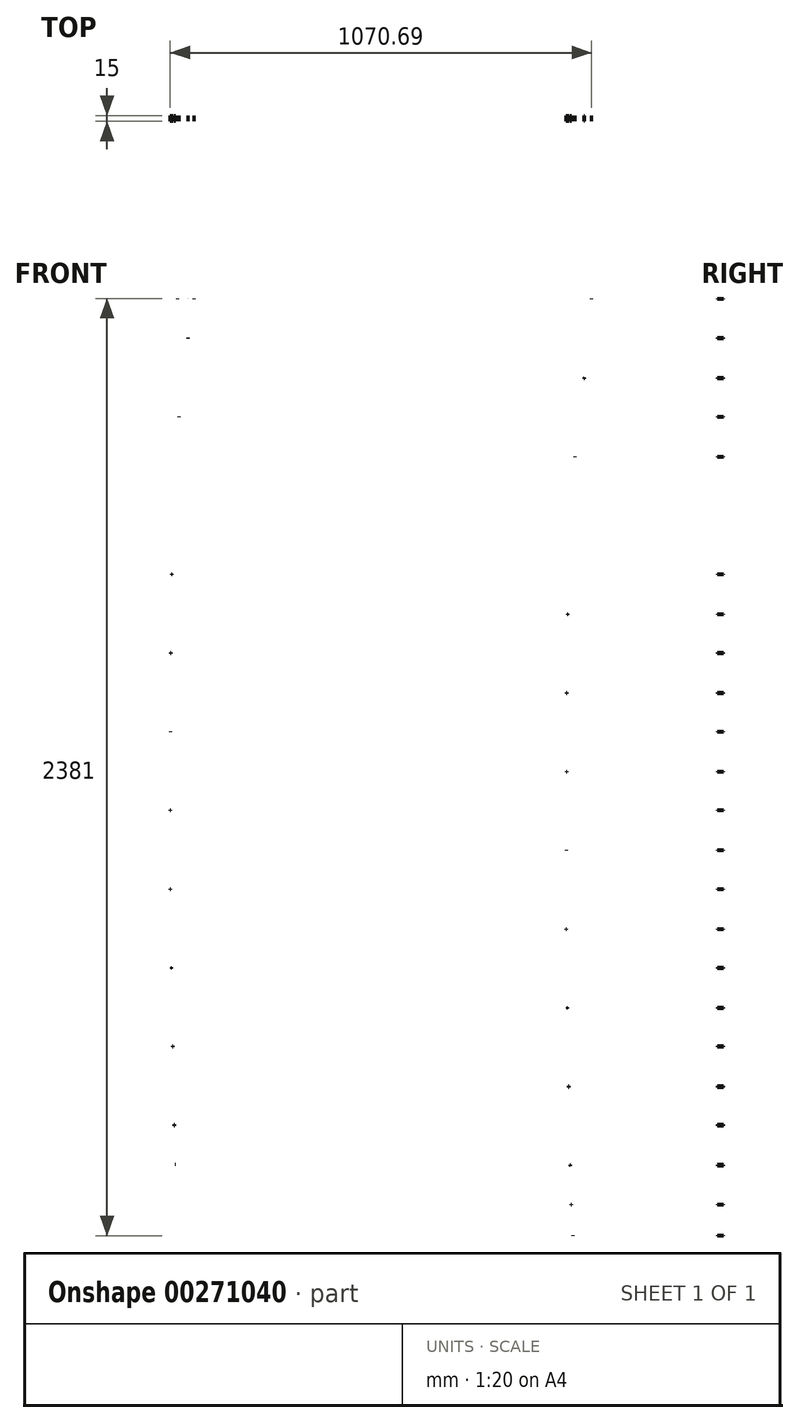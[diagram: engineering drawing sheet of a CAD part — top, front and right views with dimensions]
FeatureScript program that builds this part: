
annotation { "Feature Type Name" : "Feature", "Feature Type Description" : "" }
export const myFeature = defineFeature(function(context is Context, id is Id, definition is map)
    precondition{}
    {
        {
            var Q0;
            Q0=qCreatedBy(makeId("Front.planeOp"),FACE);
            var sketch = newSketch(context, id + "F0", { "sketchPlane" : qUnion([Q0])});
            skPoint(sketch, "E0", {"position": v(2171.02, -1257.1) * mm});
            skPoint(sketch, "E1", {"position": v(2158.22, -1157.1) * mm});
            skPoint(sketch, "E2", {"position": v(2144, -957.1) * mm});
            skPoint(sketch, "E3", {"position": v(2135.3, -757.1) * mm});
            skPoint(sketch, "E4", {"position": v(2123.54, -557.1) * mm});
            skPoint(sketch, "E5", {"position": v(2120.16, -357.1) * mm});
            skPoint(sketch, "E6", {"position": v(2123.04, -157.1) * mm});
            skPoint(sketch, "E7", {"position": v(2124, 42.9) * mm});
            skPoint(sketch, "E8", {"position": v(2129.38, 242.9) * mm});
            skPoint(sketch, "E9", {"position": v(2143.08, 442.9) * mm});
            skPoint(sketch, "E10", {"position": v(2163.32, 642.9) * mm});
            skPoint(sketch, "E11", {"position": v(2247.52, 842.9) * mm});
            skPoint(sketch, "E12", {"position": v(2193.17, 842.9) * mm});
            skPoint(sketch, "E13", {"position": v(2259.83, 942.9) * mm});
            skPoint(sketch, "E14", {"position": v(2213.09, 942.9) * mm});
            skPoint(sketch, "E15", {"position": v(2213.13, 942.9) * mm});
            skLineSegment(sketch, "E16", {"start": v(2259.83, 942.9) * mm, "end": v(2213.09, 942.9) * mm});
            skLineSegment(sketch, "E17", {"start": v(2247.52, 842.9) * mm, "end": v(2193.17, 842.9) * mm});
            skLineSegment(sketch, "E18", {"start": v(2220.35, 842.9) * mm, "end": v(2247.52, 842.9) * mm});
            skLineSegment(sketch, "E19", {"start": v(2226.63, 642.9) * mm, "end": v(2163.32, 642.9) * mm});
            skLineSegment(sketch, "E20", {"start": v(2216.48, 442.9) * mm, "end": v(2143.08, 442.9) * mm});
            skLineSegment(sketch, "E21", {"start": v(2209.4, 242.9) * mm, "end": v(2129.38, 242.9) * mm});
            skLineSegment(sketch, "E22", {"start": v(2206.83, 42.9) * mm, "end": v(2124, 42.9) * mm});
            skLineSegment(sketch, "E23", {"start": v(2206.87, -157.1) * mm, "end": v(2123.04, -157.1) * mm});
            skLineSegment(sketch, "E24", {"start": v(2206.44, -357.1) * mm, "end": v(2120.16, -357.1) * mm});
            skLineSegment(sketch, "E25", {"start": v(2205.72, -557.1) * mm, "end": v(2123.54, -557.1) * mm});
            skLineSegment(sketch, "E26", {"start": v(2208.01, -757.1) * mm, "end": v(2135.3, -757.1) * mm});
            skLineSegment(sketch, "E27", {"start": v(2210.87, -957.1) * mm, "end": v(2144, -957.1) * mm});
            skLineSegment(sketch, "E28", {"start": v(2213.68, -1157.1) * mm, "end": v(2158.22, -1157.1) * mm});
            skLineSegment(sketch, "E29", {"start": v(2214.8, -1257.1) * mm, "end": v(2171.02, -1257.1) * mm});
            skLineSegment(sketch, "E30", {"start": v(2213.09, 942.9) * mm, "end": v(2217.48, 942.9) * mm});
            skLineSegment(sketch, "E31", {"start": v(2217.48, 942.9) * mm, "end": v(2258.48, 942.9) * mm});
            skLineSegment(sketch, "E32", {"start": v(2258.48, 942.9) * mm, "end": v(2259.83, 942.9) * mm});
            skLineSegment(sketch, "E33", {"start": v(2259.75, 1046.85) * mm, "end": v(2259.75, 1077.73) * mm});
            skLineSegment(sketch, "E34", {"start": v(2273.7, 1034.65) * mm, "end": v(2273.7, 1081.36) * mm});
            skFitSpline(sketch, "E35", {"points": [v(2258.48, 942.9) * mm, v(2266.12, 990.74) * mm, v(2269.2, 1016.45) * mm, v(2266.37, 1037.52) * mm, v(2259.75, 1046.85) * mm, v(2248.64, 1041.9) * mm, v(2241.7, 1029.55) * mm, v(2229.88, 994.85) * mm, v(2217.48, 942.9) * mm], "startDerivative": vector(69.99, 299.65) * mm, "endDerivative": vector(-63.8, -297.22) * mm});
            skLineSegment(sketch, "E36", {"start": v(2193.17, 842.9) * mm, "end": v(2198.84, 842.9) * mm});
            skLineSegment(sketch, "E37", {"start": v(2198.84, 842.9) * mm, "end": v(2243.84, 842.9) * mm});
            skLineSegment(sketch, "E38", {"start": v(2243.84, 842.9) * mm, "end": v(2247.52, 842.9) * mm});
            skLineSegment(sketch, "E39", {"start": v(2226.63, 642.9) * mm, "end": v(2220.48, 642.9) * mm});
            skLineSegment(sketch, "E40", {"start": v(2220.48, 642.9) * mm, "end": v(2169.47, 642.9) * mm});
            skLineSegment(sketch, "E41", {"start": v(2169.47, 642.9) * mm, "end": v(2163.32, 642.9) * mm});
            skLineSegment(sketch, "E42", {"start": v(2209.28, 442.9) * mm, "end": v(2150.28, 442.9) * mm});
            skLineSegment(sketch, "E43", {"start": v(2150.28, 442.9) * mm, "end": v(2143.08, 442.9) * mm});
            skLineSegment(sketch, "E44", {"start": v(2201.9, 242.9) * mm, "end": v(2136.88, 242.9) * mm});
            skLineSegment(sketch, "E45", {"start": v(2136.88, 242.9) * mm, "end": v(2129.38, 242.9) * mm});
            skLineSegment(sketch, "E46", {"start": v(2199.43, 42.9) * mm, "end": v(2131.4, 42.9) * mm});
            skLineSegment(sketch, "E47", {"start": v(2131.4, 42.9) * mm, "end": v(2124, 42.9) * mm});
            skLineSegment(sketch, "E48", {"start": v(2199.16, -157.1) * mm, "end": v(2130.75, -157.1) * mm});
            skLineSegment(sketch, "E49", {"start": v(2130.75, -157.1) * mm, "end": v(2123.04, -157.1) * mm});
            skLineSegment(sketch, "E50", {"start": v(2198.3, -357.1) * mm, "end": v(2128.3, -357.1) * mm});
            skLineSegment(sketch, "E51", {"start": v(2128.3, -357.1) * mm, "end": v(2120.16, -357.1) * mm});
            skLineSegment(sketch, "E52", {"start": v(2198.13, -557.1) * mm, "end": v(2131.13, -557.1) * mm});
            skLineSegment(sketch, "E53", {"start": v(2131.13, -557.1) * mm, "end": v(2123.54, -557.1) * mm});
            skLineSegment(sketch, "E54", {"start": v(2201.35, -757.1) * mm, "end": v(2141.95, -757.1) * mm});
            skLineSegment(sketch, "E55", {"start": v(2141.95, -757.1) * mm, "end": v(2135.3, -757.1) * mm});
            skLineSegment(sketch, "E56", {"start": v(2204.43, -957.1) * mm, "end": v(2150.44, -957.1) * mm});
            skLineSegment(sketch, "E57", {"start": v(2150.44, -957.1) * mm, "end": v(2144, -957.1) * mm});
            skLineSegment(sketch, "E58", {"start": v(2208.34, -1157.1) * mm, "end": v(2163.56, -1157.1) * mm});
            skLineSegment(sketch, "E59", {"start": v(2163.56, -1157.1) * mm, "end": v(2158.22, -1157.1) * mm});
            skLineSegment(sketch, "E60", {"start": v(2210.71, -1257.1) * mm, "end": v(2175.1, -1257.1) * mm});
            skLineSegment(sketch, "E61", {"start": v(2175.1, -1257.1) * mm, "end": v(2171.02, -1257.1) * mm});
            skFitSpline(sketch, "E62", {"points": [v(2258.48, 942.9) * mm, v(2243.84, 842.9) * mm, v(2220.48, 642.9) * mm, v(2209.28, 442.9) * mm, v(2201.9, 242.9) * mm, v(2199.43, 42.9) * mm, v(2199.16, -157.1) * mm, v(2198.3, -357.1) * mm, v(2198.13, -557.1) * mm, v(2201.35, -757.1) * mm, v(2204.43, -957.1) * mm, v(2208.34, -1157.1) * mm, v(2210.71, -1257.1) * mm], "startDerivative": vector(-207.13, -1457.4) * mm, "endDerivative": vector(36.18, -1464.69) * mm});
            skFitSpline(sketch, "E63", {"points": [v(2210.71, -1257.1) * mm, v(2212.63, -1286.96) * mm, v(2214.74, -1318.98) * mm], "startDerivative": vector(3.84, -60.24) * mm, "endDerivative": vector(4.21, -63.47) * mm});
            skFitSpline(sketch, "E64", {"points": [v(2217.48, 942.9) * mm, v(2198.84, 842.9) * mm, v(2169.47, 642.9) * mm, v(2150.28, 442.9) * mm, v(2136.88, 242.9) * mm, v(2131.4, 42.9) * mm, v(2130.75, -157.1) * mm, v(2128.3, -357.1) * mm, v(2131.13, -557.1) * mm, v(2141.95, -757.1) * mm, v(2150.44, -957.1) * mm, v(2163.56, -1157.1) * mm, v(2175.1, -1257.1) * mm], "startDerivative": vector(-284.6, -1452.48) * mm, "endDerivative": vector(190.25, -1460.4) * mm});
            skFitSpline(sketch, "E65", {"points": [v(2175.1, -1257.1) * mm, v(2181.76, -1302.3) * mm, v(2183.86, -1323.32) * mm, v(2189.33, -1345.61) * mm, v(2194.8, -1356.55) * mm, v(2201.95, -1361.07) * mm, v(2209.1, -1357.4) * mm, v(2214.14, -1347.72) * mm, v(2215.4, -1335.52) * mm, v(2214.74, -1318.98) * mm], "startDerivative": vector(43.58, -267.95) * mm, "endDerivative": vector(-8.77, 152.7) * mm});
            skLineSegment(sketch, "E66", {"start": v(2258.48, 942.9) * mm, "end": v(2237.98, 942.9) * mm});
            skLineSegment(sketch, "E67", {"start": v(2131.4, 42.9) * mm, "end": v(2037.97, 42.9) * mm});
            skLineSegment(sketch, "E68", {"start": v(2037.97, 42.9) * mm, "end": v(2037.97, -1620.04) * mm});
            skLineSegment(sketch, "E69", {"start": v(2037.97, 42.9) * mm, "end": v(2037.97, 1196.3) * mm});
            skLineSegment(sketch, "E70", {"start": v(2217.48, 942.9) * mm, "end": v(2037.97, 942.9) * mm});
            skLineSegment(sketch, "E71", {"start": v(2198.84, 842.9) * mm, "end": v(2037.97, 842.9) * mm});
            skLineSegment(sketch, "E72", {"start": v(2169.47, 642.9) * mm, "end": v(2037.97, 642.9) * mm});
            skLineSegment(sketch, "E73", {"start": v(2150.28, 442.9) * mm, "end": v(2037.97, 442.9) * mm});
            skLineSegment(sketch, "E74", {"start": v(2136.88, 242.9) * mm, "end": v(2037.97, 242.9) * mm});
            skLineSegment(sketch, "E75", {"start": v(2130.75, -157.1) * mm, "end": v(2037.97, -157.1) * mm});
            skLineSegment(sketch, "E76", {"start": v(2128.3, -357.1) * mm, "end": v(2037.97, -357.1) * mm});
            skLineSegment(sketch, "E77", {"start": v(2131.13, -557.1) * mm, "end": v(2037.97, -557.1) * mm});
            skLineSegment(sketch, "E78", {"start": v(2141.95, -757.1) * mm, "end": v(2037.97, -757.1) * mm});
            skLineSegment(sketch, "E79", {"start": v(2150.44, -957.1) * mm, "end": v(2037.97, -957.1) * mm});
            skLineSegment(sketch, "E80", {"start": v(2163.56, -1157.1) * mm, "end": v(2037.97, -1157.1) * mm});
            skLineSegment(sketch, "E81", {"start": v(2175.1, -1257.1) * mm, "end": v(2037.97, -1257.1) * mm});
            skLineSegment(sketch, "E82", {"start": v(2201.95, -1361.07) * mm, "end": v(2037.97, -1361.07) * mm});
            skLineSegment(sketch, "E83", {"start": v(2037.97, -1257.1) * mm, "end": v(2037.97, -1282.1) * mm});
            skLineSegment(sketch, "E84", {"start": v(2037.97, -1282.1) * mm, "end": v(2037.97, -1311.07) * mm});
            skLineSegment(sketch, "E85", {"start": v(2037.97, -1311.07) * mm, "end": v(2037.97, -1336.07) * mm});
            skLineSegment(sketch, "E86", {"start": v(2037.97, -1336.07) * mm, "end": v(2037.97, -1361.07) * mm});
            skLineSegment(sketch, "E87", {"start": v(2037.97, -1336.07) * mm, "end": v(2186.54, -1336.07) * mm});
            skLineSegment(sketch, "E88", {"start": v(2215.4, -1335.52) * mm, "end": v(2186.54, -1336.07) * mm});
            skLineSegment(sketch, "E89", {"start": v(2259.75, 1046.85) * mm, "end": v(2247.06, 1046.85) * mm});
            skLineSegment(sketch, "E90", {"start": v(2037.97, 1046.85) * mm, "end": v(2037.97, 1021.87) * mm});
            skLineSegment(sketch, "E91", {"start": v(2037.97, 1021.87) * mm, "end": v(2238.81, 1021.87) * mm});
            skLineSegment(sketch, "E92", {"start": v(2128.3, -357.1) * mm, "end": v(2128.3, 1046.85) * mm});
            skLineSegment(sketch, "E93", {"start": v(2128.3, -357.1) * mm, "end": v(2128.3, -1361.07) * mm});
            skLineSegment(sketch, "E94", {"start": v(2128.3, -1361.07) * mm, "end": v(2128.3, 1046.85) * mm});
            skLineSegment(sketch, "E95", {"start": v(2258.48, 942.9) * mm, "end": v(2243.48, 942.9) * mm});
            skLineSegment(sketch, "E96", {"start": v(2243.84, 842.9) * mm, "end": v(2228.84, 842.9) * mm});
            skLineSegment(sketch, "E97", {"start": v(2220.48, 642.9) * mm, "end": v(2205.48, 642.9) * mm});
            skLineSegment(sketch, "E98", {"start": v(2209.28, 442.9) * mm, "end": v(2194.28, 442.9) * mm});
            skLineSegment(sketch, "E99", {"start": v(2201.9, 242.9) * mm, "end": v(2186.9, 242.9) * mm});
            skLineSegment(sketch, "E100", {"start": v(2199.43, 42.9) * mm, "end": v(2184.43, 42.9) * mm});
            skLineSegment(sketch, "E101", {"start": v(2199.16, -157.1) * mm, "end": v(2184.16, -157.1) * mm});
            skLineSegment(sketch, "E102", {"start": v(2198.3, -357.1) * mm, "end": v(2183.3, -357.1) * mm});
            skLineSegment(sketch, "E103", {"start": v(2198.13, -557.1) * mm, "end": v(2183.13, -557.1) * mm});
            skLineSegment(sketch, "E104", {"start": v(2201.35, -757.1) * mm, "end": v(2186.35, -757.1) * mm});
            skLineSegment(sketch, "E105", {"start": v(2204.43, -957.1) * mm, "end": v(2189.43, -957.1) * mm});
            skLineSegment(sketch, "E106", {"start": v(2208.34, -1157.1) * mm, "end": v(2193.34, -1157.1) * mm});
            skLineSegment(sketch, "E107", {"start": v(2210.71, -1257.1) * mm, "end": v(2195.71, -1257.1) * mm});
            skLineSegment(sketch, "E108", {"start": v(2200.4, -1335.8) * mm, "end": v(2215.4, -1335.52) * mm});
            skFitSpline(sketch, "E109", {"points": [v(2205.16, -1360.4) * mm, v(2200.4, -1335.8) * mm, v(2195.71, -1257.1) * mm, v(2193.34, -1157.1) * mm, v(2189.43, -957.1) * mm, v(2186.35, -757.1) * mm, v(2183.13, -557.1) * mm, v(2183.3, -357.1) * mm, v(2184.16, -157.1) * mm, v(2184.43, 42.9) * mm, v(2186.9, 242.9) * mm, v(2194.28, 442.9) * mm, v(2205.48, 642.9) * mm, v(2228.84, 842.9) * mm, v(2243.48, 942.9) * mm, v(2262.71, 1044.99) * mm], "startDerivative": vector(-189.04, 770.23) * mm, "endDerivative": vector(448.07, 1901.96) * mm});
            skLineSegment(sketch, "E110", {"start": v(2258.6, 943.44) * mm, "end": v(2258.88, 943.44) * mm});
            skLineSegment(sketch, "E111", {"start": v(2258.88, 943.44) * mm, "end": v(2258.88, 941.72) * mm});
            skLineSegment(sketch, "E112", {"start": v(2258.88, 941.72) * mm, "end": v(2258.3, 941.72) * mm});
            skLineSegment(sketch, "E113", {"start": v(2243.96, 843.74) * mm, "end": v(2244.2, 843.74) * mm});
            skLineSegment(sketch, "E114", {"start": v(2244.2, 843.74) * mm, "end": v(2244.2, 841.82) * mm});
            skLineSegment(sketch, "E115", {"start": v(2244.2, 841.82) * mm, "end": v(2243.7, 841.82) * mm});
            skLineSegment(sketch, "E116", {"start": v(2220.55, 643.74) * mm, "end": v(2220.94, 643.74) * mm});
            skLineSegment(sketch, "E117", {"start": v(2220.94, 643.74) * mm, "end": v(2220.94, 641.65) * mm});
            skLineSegment(sketch, "E118", {"start": v(2220.94, 641.65) * mm, "end": v(2220.37, 641.65) * mm});
            skLineSegment(sketch, "E119", {"start": v(2217.48, 942.9) * mm, "end": v(2232.48, 942.9) * mm});
            skLineSegment(sketch, "E120", {"start": v(2198.84, 842.9) * mm, "end": v(2213.84, 842.9) * mm});
            skLineSegment(sketch, "E121", {"start": v(2169.47, 642.9) * mm, "end": v(2184.47, 642.9) * mm});
            skLineSegment(sketch, "E122", {"start": v(2150.28, 442.9) * mm, "end": v(2165.28, 442.9) * mm});
            skLineSegment(sketch, "E123", {"start": v(2136.88, 242.9) * mm, "end": v(2151.88, 242.9) * mm});
            skLineSegment(sketch, "E124", {"start": v(2131.4, 42.9) * mm, "end": v(2146.4, 42.9) * mm});
            skLineSegment(sketch, "E125", {"start": v(2130.75, -157.1) * mm, "end": v(2145.75, -157.1) * mm});
            skLineSegment(sketch, "E126", {"start": v(2128.3, -357.1) * mm, "end": v(2143.3, -357.1) * mm});
            skLineSegment(sketch, "E127", {"start": v(2131.13, -557.1) * mm, "end": v(2146.13, -557.1) * mm});
            skLineSegment(sketch, "E128", {"start": v(2141.95, -757.1) * mm, "end": v(2156.95, -757.1) * mm});
            skLineSegment(sketch, "E129", {"start": v(2150.44, -957.1) * mm, "end": v(2165.44, -957.1) * mm});
            skLineSegment(sketch, "E130", {"start": v(2163.56, -1157.1) * mm, "end": v(2178.56, -1157.1) * mm});
            skLineSegment(sketch, "E131", {"start": v(2175.1, -1257.1) * mm, "end": v(2190.1, -1257.1) * mm});
            skLineSegment(sketch, "E132", {"start": v(2186.54, -1336.07) * mm, "end": v(2201.53, -1335.78) * mm});
            skFitSpline(sketch, "E133", {"points": [v(2205.16, -1360.4) * mm, v(2201.53, -1335.78) * mm, v(2190.1, -1257.1) * mm, v(2178.56, -1157.1) * mm, v(2165.44, -957.1) * mm, v(2156.95, -757.1) * mm, v(2146.13, -557.1) * mm, v(2143.3, -357.1) * mm, v(2145.75, -157.1) * mm, v(2146.4, 42.9) * mm, v(2151.88, 242.9) * mm, v(2165.28, 442.9) * mm, v(2184.47, 642.9) * mm, v(2213.84, 842.9) * mm, v(2232.48, 942.9) * mm, v(2262.71, 1044.99) * mm], "startDerivative": vector(-114.37, 778.22) * mm, "endDerivative": vector(603.08, 1884.97) * mm});
            skLineSegment(sketch, "E134", {"start": v(2217.66, 943.77) * mm, "end": v(2216.66, 943.77) * mm});
            skLineSegment(sketch, "E135", {"start": v(2216.66, 943.77) * mm, "end": v(2216.66, 941.63) * mm});
            skLineSegment(sketch, "E136", {"start": v(2216.66, 941.63) * mm, "end": v(2217.23, 941.63) * mm});
            skLineSegment(sketch, "E137", {"start": v(2243.44, 942.9) * mm, "end": v(2243.42, 942.9) * mm});
            skLineSegment(sketch, "E138", {"start": v(2243.42, 942.9) * mm, "end": v(2243.42, 942.88) * mm});
            skLineSegment(sketch, "E139", {"start": v(2243.42, 942.88) * mm, "end": v(2243.43, 942.88) * mm});
            skLineSegment(sketch, "E140", {"start": v(2243.48, 942.9) * mm, "end": v(2243.48, 942.92) * mm});
            skLineSegment(sketch, "E141", {"start": v(2243.48, 942.92) * mm, "end": v(2243.45, 942.92) * mm});
            skLineSegment(sketch, "E142", {"start": v(2243.45, 942.92) * mm, "end": v(2243.45, 942.86) * mm});
            skLineSegment(sketch, "E143", {"start": v(2243.45, 942.86) * mm, "end": v(2243.48, 942.86) * mm});
            skLineSegment(sketch, "E144", {"start": v(2243.48, 942.86) * mm, "end": v(2243.48, 942.9) * mm});
            skLineSegment(sketch, "E145", {"start": v(2262.44, 1044.14) * mm, "end": v(2262.5, 1044.06) * mm});
            skLineSegment(sketch, "E146", {"start": v(2209.28, 442.9) * mm, "end": v(2209.38, 442.9) * mm});
            skLineSegment(sketch, "E147", {"start": v(2209.38, 442.9) * mm, "end": v(2209.38, 442.64) * mm});
            skLineSegment(sketch, "E148", {"start": v(2209.38, 442.64) * mm, "end": v(2209.27, 442.64) * mm});
            skLineSegment(sketch, "E149", {"start": v(2209.38, 442.9) * mm, "end": v(2209.38, 443.1) * mm});
            skLineSegment(sketch, "E150", {"start": v(2209.38, 443.1) * mm, "end": v(2209.29, 443.1) * mm});
            skLineSegment(sketch, "E151", {"start": v(2202.84, 242.9) * mm, "end": v(2202.84, 242.19) * mm});
            skLineSegment(sketch, "E152", {"start": v(2202.84, 242.19) * mm, "end": v(2201.7, 242.19) * mm});
            skLineSegment(sketch, "E153", {"start": v(2202.84, 242.9) * mm, "end": v(2202.84, 243.54) * mm});
            skLineSegment(sketch, "E154", {"start": v(2202.84, 243.54) * mm, "end": v(2201.6, 243.54) * mm});
            skLineSegment(sketch, "E155", {"start": v(2199.44, 44.15) * mm, "end": v(2200.68, 44.15) * mm});
            skLineSegment(sketch, "E156", {"start": v(2200.68, 44.15) * mm, "end": v(2200.68, 41.57) * mm});
            skLineSegment(sketch, "E157", {"start": v(2200.68, 41.57) * mm, "end": v(2197.93, 41.57) * mm});
            skLineSegment(sketch, "E158", {"start": v(2198.55, -156.57) * mm, "end": v(2199.5, -156.57) * mm});
            skLineSegment(sketch, "E159", {"start": v(2199.5, -156.57) * mm, "end": v(2199.5, -157.6) * mm});
            skLineSegment(sketch, "E160", {"start": v(2199.5, -157.6) * mm, "end": v(2198.3, -157.6) * mm});
            skLineSegment(sketch, "E161", {"start": v(2198.3, -357.42) * mm, "end": v(2198.68, -357.42) * mm});
            skLineSegment(sketch, "E162", {"start": v(2198.68, -357.42) * mm, "end": v(2198.72, -356.49) * mm});
            skLineSegment(sketch, "E163", {"start": v(2198.72, -356.49) * mm, "end": v(2198.31, -356.5) * mm});
            skLineSegment(sketch, "E164", {"start": v(2198.14, -558.04) * mm, "end": v(2199.17, -558.04) * mm});
            skLineSegment(sketch, "E165", {"start": v(2199.17, -558.04) * mm, "end": v(2199.17, -554.96) * mm});
            skLineSegment(sketch, "E166", {"start": v(2199.17, -554.96) * mm, "end": v(2198.13, -554.96) * mm});
            skLineSegment(sketch, "E167", {"start": v(2201.34, -756.37) * mm, "end": v(2201.8, -756.37) * mm});
            skLineSegment(sketch, "E168", {"start": v(2201.8, -756.37) * mm, "end": v(2201.8, -758.47) * mm});
            skLineSegment(sketch, "E169", {"start": v(2201.8, -758.47) * mm, "end": v(2200.68, -758.51) * mm});
            skLineSegment(sketch, "E170", {"start": v(2201.34, -756.37) * mm, "end": v(2201.18, -756.37) * mm});
            skLineSegment(sketch, "E171", {"start": v(2204.41, -956.06) * mm, "end": v(2205.02, -956.06) * mm});
            skLineSegment(sketch, "E172", {"start": v(2205.02, -956.06) * mm, "end": v(2205.02, -958.88) * mm});
            skLineSegment(sketch, "E173", {"start": v(2205.02, -958.88) * mm, "end": v(2203.85, -958.94) * mm});
            skLineSegment(sketch, "E174", {"start": v(2208.3, -1155.68) * mm, "end": v(2209.33, -1155.68) * mm});
            skLineSegment(sketch, "E175", {"start": v(2209.33, -1155.68) * mm, "end": v(2209.33, -1159.24) * mm});
            skLineSegment(sketch, "E176", {"start": v(2209.33, -1159.24) * mm, "end": v(2207.47, -1159.24) * mm});
            skLineSegment(sketch, "E177", {"start": v(2210.69, -1256.19) * mm, "end": v(2211.33, -1256.19) * mm});
            skLineSegment(sketch, "E178", {"start": v(2211.33, -1256.19) * mm, "end": v(2211.33, -1258.17) * mm});
            skLineSegment(sketch, "E179", {"start": v(2211.33, -1258.17) * mm, "end": v(2210.43, -1258.24) * mm});
            skLineSegment(sketch, "E180", {"start": v(2215.4, -1334.95) * mm, "end": v(2215.92, -1334.95) * mm});
            skLineSegment(sketch, "E181", {"start": v(2215.92, -1334.95) * mm, "end": v(2215.86, -1335.93) * mm});
            skLineSegment(sketch, "E182", {"start": v(2215.86, -1335.93) * mm, "end": v(2215.18, -1336.06) * mm});
            skLineSegment(sketch, "E183", {"start": v(1774.36, 1162.64) * mm, "end": v(1812.36, 1162.64) * mm});
            skLineSegment(sketch, "E184", {"start": v(1756.32, 262.64) * mm, "end": v(1688.3, 262.64) * mm});
            skLineSegment(sketch, "E185", {"start": v(1755.73, 1062.64) * mm, "end": v(1798.74, 1062.64) * mm});
            skLineSegment(sketch, "E186", {"start": v(1772.3, -1115.77) * mm, "end": v(1743.42, -1116.32) * mm});
            skPoint(sketch, "E187", {"position": v(4938.92, -952.74) * mm});
            skPoint(sketch, "E188", {"position": v(4926.12, -852.74) * mm});
            skPoint(sketch, "E189", {"position": v(4911.9, -652.74) * mm});
            skPoint(sketch, "E190", {"position": v(4903.19, -452.74) * mm});
            skPoint(sketch, "E191", {"position": v(4891.44, -252.74) * mm});
            skPoint(sketch, "E192", {"position": v(4888.06, -52.74) * mm});
            skPoint(sketch, "E193", {"position": v(4890.94, 147.26) * mm});
            skPoint(sketch, "E194", {"position": v(4891.9, 347.26) * mm});
            skPoint(sketch, "E195", {"position": v(4897.28, 547.26) * mm});
            skPoint(sketch, "E196", {"position": v(4910.97, 747.26) * mm});
            skPoint(sketch, "E197", {"position": v(4931.22, 947.26) * mm});
            skPoint(sketch, "E198", {"position": v(5015.42, 1147.26) * mm});
            skPoint(sketch, "E199", {"position": v(4961.06, 1147.26) * mm});
            skPoint(sketch, "E200", {"position": v(5027.72, 1247.26) * mm});
            skPoint(sketch, "E201", {"position": v(4980.99, 1247.26) * mm});
            skPoint(sketch, "E202", {"position": v(4981.02, 1247.26) * mm});
            skLineSegment(sketch, "E203", {"start": v(5027.72, 1247.26) * mm, "end": v(4980.99, 1247.26) * mm});
            skLineSegment(sketch, "E204", {"start": v(5015.42, 1147.26) * mm, "end": v(4961.06, 1147.26) * mm});
            skLineSegment(sketch, "E205", {"start": v(4988.24, 1147.26) * mm, "end": v(5015.42, 1147.26) * mm});
            skLineSegment(sketch, "E206", {"start": v(4994.52, 947.26) * mm, "end": v(4931.22, 947.26) * mm});
            skLineSegment(sketch, "E207", {"start": v(4984.38, 747.26) * mm, "end": v(4910.97, 747.26) * mm});
            skLineSegment(sketch, "E208", {"start": v(4977.3, 547.26) * mm, "end": v(4897.28, 547.26) * mm});
            skLineSegment(sketch, "E209", {"start": v(4974.73, 347.26) * mm, "end": v(4891.9, 347.26) * mm});
            skLineSegment(sketch, "E210", {"start": v(4974.76, 147.26) * mm, "end": v(4890.94, 147.26) * mm});
            skLineSegment(sketch, "E211", {"start": v(4974.33, -52.74) * mm, "end": v(4888.06, -52.74) * mm});
            skLineSegment(sketch, "E212", {"start": v(4973.62, -252.74) * mm, "end": v(4891.44, -252.74) * mm});
            skLineSegment(sketch, "E213", {"start": v(4975.91, -452.74) * mm, "end": v(4903.19, -452.74) * mm});
            skLineSegment(sketch, "E214", {"start": v(4978.77, -652.74) * mm, "end": v(4911.9, -652.74) * mm});
            skLineSegment(sketch, "E215", {"start": v(4981.58, -852.74) * mm, "end": v(4926.12, -852.74) * mm});
            skLineSegment(sketch, "E216", {"start": v(4982.7, -952.74) * mm, "end": v(4938.92, -952.74) * mm});
            skLineSegment(sketch, "E217", {"start": v(4980.99, 1247.26) * mm, "end": v(4985.37, 1247.26) * mm});
            skLineSegment(sketch, "E218", {"start": v(4985.37, 1247.26) * mm, "end": v(5026.37, 1247.26) * mm});
            skLineSegment(sketch, "E219", {"start": v(5026.37, 1247.26) * mm, "end": v(5027.72, 1247.26) * mm});
            skLineSegment(sketch, "E220", {"start": v(5027.65, 1351.22) * mm, "end": v(5027.65, 1382.1) * mm});
            skLineSegment(sketch, "E221", {"start": v(5041.6, 1339) * mm, "end": v(5041.6, 1385.72) * mm});
            skLineSegment(sketch, "E222", {"start": v(4961.06, 1147.26) * mm, "end": v(4966.74, 1147.26) * mm});
            skLineSegment(sketch, "E223", {"start": v(4966.74, 1147.26) * mm, "end": v(5011.74, 1147.26) * mm});
            skLineSegment(sketch, "E224", {"start": v(5011.74, 1147.26) * mm, "end": v(5015.42, 1147.26) * mm});
            skLineSegment(sketch, "E225", {"start": v(4994.52, 947.26) * mm, "end": v(4988.37, 947.26) * mm});
            skLineSegment(sketch, "E226", {"start": v(4988.37, 947.26) * mm, "end": v(4937.37, 947.26) * mm});
            skLineSegment(sketch, "E227", {"start": v(4937.37, 947.26) * mm, "end": v(4931.22, 947.26) * mm});
            skLineSegment(sketch, "E228", {"start": v(4977.18, 747.26) * mm, "end": v(4918.17, 747.26) * mm});
            skLineSegment(sketch, "E229", {"start": v(4918.17, 747.26) * mm, "end": v(4910.97, 747.26) * mm});
            skLineSegment(sketch, "E230", {"start": v(4969.8, 547.26) * mm, "end": v(4904.78, 547.26) * mm});
            skLineSegment(sketch, "E231", {"start": v(4904.78, 547.26) * mm, "end": v(4897.28, 547.26) * mm});
            skLineSegment(sketch, "E232", {"start": v(4967.33, 347.26) * mm, "end": v(4899.3, 347.26) * mm});
            skLineSegment(sketch, "E233", {"start": v(4899.3, 347.26) * mm, "end": v(4891.9, 347.26) * mm});
            skLineSegment(sketch, "E234", {"start": v(4967.05, 147.26) * mm, "end": v(4898.65, 147.26) * mm});
            skLineSegment(sketch, "E235", {"start": v(4898.65, 147.26) * mm, "end": v(4890.94, 147.26) * mm});
            skLineSegment(sketch, "E236", {"start": v(4966.2, -52.74) * mm, "end": v(4896.2, -52.74) * mm});
            skLineSegment(sketch, "E237", {"start": v(4896.2, -52.74) * mm, "end": v(4888.06, -52.74) * mm});
            skLineSegment(sketch, "E238", {"start": v(4966.03, -252.74) * mm, "end": v(4899.03, -252.74) * mm});
            skLineSegment(sketch, "E239", {"start": v(4899.03, -252.74) * mm, "end": v(4891.44, -252.74) * mm});
            skLineSegment(sketch, "E240", {"start": v(4969.25, -452.74) * mm, "end": v(4909.85, -452.74) * mm});
            skLineSegment(sketch, "E241", {"start": v(4909.85, -452.74) * mm, "end": v(4903.19, -452.74) * mm});
            skLineSegment(sketch, "E242", {"start": v(4972.33, -652.74) * mm, "end": v(4918.34, -652.74) * mm});
            skLineSegment(sketch, "E243", {"start": v(4918.34, -652.74) * mm, "end": v(4911.9, -652.74) * mm});
            skLineSegment(sketch, "E244", {"start": v(4976.24, -852.74) * mm, "end": v(4931.46, -852.74) * mm});
            skLineSegment(sketch, "E245", {"start": v(4931.46, -852.74) * mm, "end": v(4926.12, -852.74) * mm});
            skLineSegment(sketch, "E246", {"start": v(4978.61, -952.74) * mm, "end": v(4943, -952.74) * mm});
            skLineSegment(sketch, "E247", {"start": v(4943, -952.74) * mm, "end": v(4938.92, -952.74) * mm});
            skFitSpline(sketch, "E248", {"points": [v(5026.37, 1247.26) * mm, v(5011.74, 1147.26) * mm, v(4988.37, 947.26) * mm, v(4977.18, 747.26) * mm, v(4969.8, 547.26) * mm, v(4967.33, 347.26) * mm, v(4967.05, 147.26) * mm, v(4966.2, -52.74) * mm, v(4966.03, -252.74) * mm, v(4969.25, -452.74) * mm, v(4972.33, -652.74) * mm, v(4976.24, -852.74) * mm, v(4978.61, -952.74) * mm], "startDerivative": vector(-207.13, -1457.4) * mm, "endDerivative": vector(36.18, -1464.69) * mm});
            skFitSpline(sketch, "E249", {"points": [v(4985.37, 1247.26) * mm, v(4966.74, 1147.26) * mm, v(4937.37, 947.26) * mm, v(4918.17, 747.26) * mm, v(4904.78, 547.26) * mm, v(4899.3, 347.26) * mm, v(4898.65, 147.26) * mm, v(4896.2, -52.74) * mm, v(4899.03, -252.74) * mm, v(4909.85, -452.74) * mm, v(4918.34, -652.74) * mm, v(4931.46, -852.74) * mm, v(4943, -952.74) * mm], "startDerivative": vector(-284.6, -1452.48) * mm, "endDerivative": vector(190.25, -1460.4) * mm});
            skLineSegment(sketch, "E250", {"start": v(5026.37, 1247.26) * mm, "end": v(5005.87, 1247.26) * mm});
            skLineSegment(sketch, "E251", {"start": v(4899.3, 347.26) * mm, "end": v(4805.87, 347.26) * mm});
            skLineSegment(sketch, "E252", {"start": v(4805.87, 347.26) * mm, "end": v(4805.87, -1315.68) * mm});
            skLineSegment(sketch, "E253", {"start": v(4805.87, 347.26) * mm, "end": v(4805.87, 1500.66) * mm});
            skLineSegment(sketch, "E254", {"start": v(4985.37, 1247.26) * mm, "end": v(4805.87, 1247.26) * mm});
            skLineSegment(sketch, "E255", {"start": v(4966.74, 1147.26) * mm, "end": v(4805.87, 1147.26) * mm});
            skLineSegment(sketch, "E256", {"start": v(4937.37, 947.26) * mm, "end": v(4805.87, 947.26) * mm});
            skLineSegment(sketch, "E257", {"start": v(4918.17, 747.26) * mm, "end": v(4805.87, 747.26) * mm});
            skLineSegment(sketch, "E258", {"start": v(4904.78, 547.26) * mm, "end": v(4805.87, 547.26) * mm});
            skLineSegment(sketch, "E259", {"start": v(4898.65, 147.26) * mm, "end": v(4805.87, 147.26) * mm});
            skLineSegment(sketch, "E260", {"start": v(4896.2, -52.74) * mm, "end": v(4805.87, -52.74) * mm});
            skLineSegment(sketch, "E261", {"start": v(4899.03, -252.74) * mm, "end": v(4805.87, -252.74) * mm});
            skLineSegment(sketch, "E262", {"start": v(4909.85, -452.74) * mm, "end": v(4805.87, -452.74) * mm});
            skLineSegment(sketch, "E263", {"start": v(4918.34, -652.74) * mm, "end": v(4805.87, -652.74) * mm});
            skLineSegment(sketch, "E264", {"start": v(4931.46, -852.74) * mm, "end": v(4805.87, -852.74) * mm});
            skLineSegment(sketch, "E265", {"start": v(4943, -952.74) * mm, "end": v(4805.87, -952.74) * mm});
            skLineSegment(sketch, "E266", {"start": v(4969.84, -1056.7) * mm, "end": v(4805.87, -1056.7) * mm});
            skLineSegment(sketch, "E267", {"start": v(4805.87, -952.74) * mm, "end": v(4805.87, -977.74) * mm});
            skLineSegment(sketch, "E268", {"start": v(4805.87, -977.74) * mm, "end": v(4805.87, -1006.7) * mm});
            skLineSegment(sketch, "E269", {"start": v(4805.87, -1006.7) * mm, "end": v(4805.87, -1031.7) * mm});
            skLineSegment(sketch, "E270", {"start": v(4805.87, -1031.7) * mm, "end": v(4805.87, -1056.7) * mm});
            skLineSegment(sketch, "E271", {"start": v(4805.87, -1031.7) * mm, "end": v(4954.43, -1031.7) * mm});
            skLineSegment(sketch, "E272", {"start": v(4983.3, -1031.16) * mm, "end": v(4954.43, -1031.7) * mm});
            skLineSegment(sketch, "E273", {"start": v(5027.65, 1351.22) * mm, "end": v(4805.87, 1351.22) * mm});
            skLineSegment(sketch, "E274", {"start": v(4805.87, 1351.22) * mm, "end": v(4805.87, 1326.23) * mm});
            skLineSegment(sketch, "E275", {"start": v(4805.87, 1326.23) * mm, "end": v(5006.7, 1326.23) * mm});
            skLineSegment(sketch, "E276", {"start": v(4896.2, -52.74) * mm, "end": v(4896.2, 1351.22) * mm});
            skLineSegment(sketch, "E277", {"start": v(4896.2, -52.74) * mm, "end": v(4896.2, -1056.7) * mm});
            skLineSegment(sketch, "E278", {"start": v(4896.2, -1056.7) * mm, "end": v(4896.2, 1351.22) * mm});
            skLineSegment(sketch, "E279", {"start": v(5026.37, 1247.26) * mm, "end": v(5011.37, 1247.26) * mm});
            skLineSegment(sketch, "E280", {"start": v(5011.74, 1147.26) * mm, "end": v(4996.74, 1147.26) * mm});
            skLineSegment(sketch, "E281", {"start": v(4988.37, 947.26) * mm, "end": v(4973.37, 947.26) * mm});
            skLineSegment(sketch, "E282", {"start": v(4977.18, 747.26) * mm, "end": v(4962.18, 747.26) * mm});
            skLineSegment(sketch, "E283", {"start": v(4969.8, 547.26) * mm, "end": v(4954.8, 547.26) * mm});
            skLineSegment(sketch, "E284", {"start": v(4967.33, 347.26) * mm, "end": v(4952.33, 347.26) * mm});
            skLineSegment(sketch, "E285", {"start": v(4967.05, 147.26) * mm, "end": v(4952.05, 147.26) * mm});
            skLineSegment(sketch, "E286", {"start": v(4966.2, -52.74) * mm, "end": v(4951.2, -52.74) * mm});
            skLineSegment(sketch, "E287", {"start": v(4966.03, -252.74) * mm, "end": v(4951.03, -252.74) * mm});
            skLineSegment(sketch, "E288", {"start": v(4969.25, -452.74) * mm, "end": v(4954.25, -452.74) * mm});
            skLineSegment(sketch, "E289", {"start": v(4972.33, -652.74) * mm, "end": v(4957.33, -652.74) * mm});
            skLineSegment(sketch, "E290", {"start": v(4976.24, -852.74) * mm, "end": v(4961.24, -852.74) * mm});
            skLineSegment(sketch, "E291", {"start": v(4978.61, -952.74) * mm, "end": v(4963.61, -952.74) * mm});
            skLineSegment(sketch, "E292", {"start": v(4968.3, -1031.44) * mm, "end": v(4983.3, -1031.16) * mm});
            skLineSegment(sketch, "E293", {"start": v(5026.5, 1247.8) * mm, "end": v(5026.78, 1247.8) * mm});
            skLineSegment(sketch, "E294", {"start": v(5026.78, 1247.8) * mm, "end": v(5026.78, 1246.08) * mm});
            skLineSegment(sketch, "E295", {"start": v(5026.78, 1246.08) * mm, "end": v(5026.2, 1246.08) * mm});
            skLineSegment(sketch, "E296", {"start": v(5011.86, 1148.1) * mm, "end": v(5012.1, 1148.1) * mm});
            skLineSegment(sketch, "E297", {"start": v(5012.1, 1148.1) * mm, "end": v(5012.1, 1146.19) * mm});
            skLineSegment(sketch, "E298", {"start": v(5012.1, 1146.19) * mm, "end": v(5011.59, 1146.19) * mm});
            skLineSegment(sketch, "E299", {"start": v(4988.45, 948.1) * mm, "end": v(4988.84, 948.1) * mm});
            skLineSegment(sketch, "E300", {"start": v(4988.84, 948.1) * mm, "end": v(4988.84, 946.01) * mm});
            skLineSegment(sketch, "E301", {"start": v(4988.84, 946.01) * mm, "end": v(4988.27, 946.01) * mm});
            skLineSegment(sketch, "E302", {"start": v(4985.37, 1247.26) * mm, "end": v(5000.37, 1247.26) * mm});
            skLineSegment(sketch, "E303", {"start": v(4966.74, 1147.26) * mm, "end": v(4981.74, 1147.26) * mm});
            skLineSegment(sketch, "E304", {"start": v(4937.37, 947.26) * mm, "end": v(4952.37, 947.26) * mm});
            skLineSegment(sketch, "E305", {"start": v(4918.17, 747.26) * mm, "end": v(4933.17, 747.26) * mm});
            skLineSegment(sketch, "E306", {"start": v(4904.78, 547.26) * mm, "end": v(4919.78, 547.26) * mm});
            skLineSegment(sketch, "E307", {"start": v(4899.3, 347.26) * mm, "end": v(4914.3, 347.26) * mm});
            skLineSegment(sketch, "E308", {"start": v(4898.65, 147.26) * mm, "end": v(4913.65, 147.26) * mm});
            skLineSegment(sketch, "E309", {"start": v(4896.2, -52.74) * mm, "end": v(4911.2, -52.74) * mm});
            skLineSegment(sketch, "E310", {"start": v(4899.03, -252.74) * mm, "end": v(4914.03, -252.74) * mm});
            skLineSegment(sketch, "E311", {"start": v(4909.85, -452.74) * mm, "end": v(4924.85, -452.74) * mm});
            skLineSegment(sketch, "E312", {"start": v(4918.34, -652.74) * mm, "end": v(4933.34, -652.74) * mm});
            skLineSegment(sketch, "E313", {"start": v(4931.46, -852.74) * mm, "end": v(4946.46, -852.74) * mm});
            skLineSegment(sketch, "E314", {"start": v(4943, -952.74) * mm, "end": v(4958, -952.74) * mm});
            skLineSegment(sketch, "E315", {"start": v(4954.43, -1031.7) * mm, "end": v(4969.43, -1031.42) * mm});
            skLineSegment(sketch, "E316", {"start": v(4985.56, 1248.14) * mm, "end": v(4984.56, 1248.14) * mm});
            skLineSegment(sketch, "E317", {"start": v(4984.56, 1248.14) * mm, "end": v(4984.56, 1246) * mm});
            skLineSegment(sketch, "E318", {"start": v(4984.56, 1246) * mm, "end": v(4985.13, 1246) * mm});
            skLineSegment(sketch, "E319", {"start": v(5011.33, 1247.26) * mm, "end": v(5011.31, 1247.26) * mm});
            skLineSegment(sketch, "E320", {"start": v(5011.31, 1247.26) * mm, "end": v(5011.31, 1247.24) * mm});
            skLineSegment(sketch, "E321", {"start": v(5011.31, 1247.24) * mm, "end": v(5011.33, 1247.24) * mm});
            skLineSegment(sketch, "E322", {"start": v(5011.37, 1247.26) * mm, "end": v(5011.37, 1247.28) * mm});
            skLineSegment(sketch, "E323", {"start": v(5011.37, 1247.28) * mm, "end": v(5011.35, 1247.28) * mm});
            skLineSegment(sketch, "E324", {"start": v(5011.35, 1247.28) * mm, "end": v(5011.35, 1247.22) * mm});
            skLineSegment(sketch, "E325", {"start": v(5011.35, 1247.22) * mm, "end": v(5011.37, 1247.22) * mm});
            skLineSegment(sketch, "E326", {"start": v(5011.37, 1247.22) * mm, "end": v(5011.37, 1247.26) * mm});
            skLineSegment(sketch, "E327", {"start": v(5030.34, 1348.5) * mm, "end": v(5030.4, 1348.43) * mm});
            skLineSegment(sketch, "E328", {"start": v(4977.18, 747.26) * mm, "end": v(4977.28, 747.26) * mm});
            skLineSegment(sketch, "E329", {"start": v(4977.28, 747.26) * mm, "end": v(4977.28, 747) * mm});
            skLineSegment(sketch, "E330", {"start": v(4977.28, 747) * mm, "end": v(4977.17, 747) * mm});
            skLineSegment(sketch, "E331", {"start": v(4977.28, 747.26) * mm, "end": v(4977.28, 747.46) * mm});
            skLineSegment(sketch, "E332", {"start": v(4977.28, 747.46) * mm, "end": v(4977.18, 747.46) * mm});
            skLineSegment(sketch, "E333", {"start": v(4970.74, 547.26) * mm, "end": v(4970.74, 546.55) * mm});
            skLineSegment(sketch, "E334", {"start": v(4970.74, 546.55) * mm, "end": v(4969.59, 546.55) * mm});
            skLineSegment(sketch, "E335", {"start": v(4970.74, 547.26) * mm, "end": v(4970.74, 547.9) * mm});
            skLineSegment(sketch, "E336", {"start": v(4970.74, 547.9) * mm, "end": v(4969.5, 547.9) * mm});
            skLineSegment(sketch, "E337", {"start": v(4967.33, 348.51) * mm, "end": v(4968.58, 348.51) * mm});
            skLineSegment(sketch, "E338", {"start": v(4968.58, 348.51) * mm, "end": v(4968.58, 345.93) * mm});
            skLineSegment(sketch, "E339", {"start": v(4968.58, 345.93) * mm, "end": v(4965.83, 345.93) * mm});
            skLineSegment(sketch, "E340", {"start": v(4966.45, 147.79) * mm, "end": v(4967.39, 147.79) * mm});
            skLineSegment(sketch, "E341", {"start": v(4967.39, 147.79) * mm, "end": v(4967.39, 146.77) * mm});
            skLineSegment(sketch, "E342", {"start": v(4967.39, 146.77) * mm, "end": v(4966.2, 146.77) * mm});
            skLineSegment(sketch, "E343", {"start": v(4966.2, -53.06) * mm, "end": v(4966.58, -53.06) * mm});
            skLineSegment(sketch, "E344", {"start": v(4966.58, -53.06) * mm, "end": v(4966.62, -52.13) * mm});
            skLineSegment(sketch, "E345", {"start": v(4966.62, -52.13) * mm, "end": v(4966.2, -52.15) * mm});
            skLineSegment(sketch, "E346", {"start": v(4966.04, -253.68) * mm, "end": v(4967.07, -253.68) * mm});
            skLineSegment(sketch, "E347", {"start": v(4967.07, -253.68) * mm, "end": v(4967.07, -250.6) * mm});
            skLineSegment(sketch, "E348", {"start": v(4967.07, -250.6) * mm, "end": v(4966.03, -250.6) * mm});
            skLineSegment(sketch, "E349", {"start": v(4969.24, -452.01) * mm, "end": v(4969.7, -452.01) * mm});
            skLineSegment(sketch, "E350", {"start": v(4969.7, -452.01) * mm, "end": v(4969.7, -454.1) * mm});
            skLineSegment(sketch, "E351", {"start": v(4969.7, -454.1) * mm, "end": v(4968.57, -454.15) * mm});
            skLineSegment(sketch, "E352", {"start": v(4969.24, -452.01) * mm, "end": v(4969.08, -452.01) * mm});
            skLineSegment(sketch, "E353", {"start": v(4972.3, -651.7) * mm, "end": v(4972.92, -651.7) * mm});
            skLineSegment(sketch, "E354", {"start": v(4972.92, -651.7) * mm, "end": v(4972.92, -654.52) * mm});
            skLineSegment(sketch, "E355", {"start": v(4972.92, -654.52) * mm, "end": v(4971.75, -654.58) * mm});
            skLineSegment(sketch, "E356", {"start": v(4976.2, -851.32) * mm, "end": v(4977.23, -851.32) * mm});
            skLineSegment(sketch, "E357", {"start": v(4977.23, -851.32) * mm, "end": v(4977.23, -854.87) * mm});
            skLineSegment(sketch, "E358", {"start": v(4977.23, -854.87) * mm, "end": v(4975.36, -854.87) * mm});
            skLineSegment(sketch, "E359", {"start": v(4978.59, -951.83) * mm, "end": v(4979.22, -951.83) * mm});
            skLineSegment(sketch, "E360", {"start": v(4979.22, -951.83) * mm, "end": v(4979.23, -953.81) * mm});
            skLineSegment(sketch, "E361", {"start": v(4979.23, -953.81) * mm, "end": v(4978.33, -953.88) * mm});
            skLineSegment(sketch, "E362", {"start": v(4983.3, -1030.58) * mm, "end": v(4983.82, -1030.58) * mm});
            skLineSegment(sketch, "E363", {"start": v(4983.82, -1030.58) * mm, "end": v(4983.76, -1031.57) * mm});
            skLineSegment(sketch, "E364", {"start": v(4983.76, -1031.57) * mm, "end": v(4983.08, -1031.7) * mm});
            skFitSpline(sketch, "E365", {"points": [v(4973.06, -1056.03) * mm, v(4969.43, -1031.42) * mm, v(4958, -952.74) * mm, v(4946.46, -852.74) * mm, v(4933.34, -652.74) * mm, v(4924.85, -452.74) * mm, v(4914.03, -252.74) * mm, v(4911.2, -52.74) * mm, v(4913.65, 147.26) * mm, v(4914.3, 347.26) * mm, v(4919.78, 547.26) * mm, v(4933.17, 747.26) * mm, v(4952.37, 947.26) * mm, v(4981.74, 1147.26) * mm, v(5000.37, 1247.26) * mm, v(5030.6, 1349.35) * mm], "startDerivative": vector(-114.37, 778.22) * mm, "endDerivative": vector(603.08, 1884.97) * mm});
            skFitSpline(sketch, "E366", {"points": [v(4973.06, -1056.03) * mm, v(4968.3, -1031.44) * mm, v(4963.61, -952.74) * mm, v(4961.24, -852.74) * mm, v(4957.33, -652.74) * mm, v(4954.25, -452.74) * mm, v(4951.03, -252.74) * mm, v(4951.2, -52.74) * mm, v(4952.05, 147.26) * mm, v(4952.33, 347.26) * mm, v(4954.8, 547.26) * mm, v(4962.18, 747.26) * mm, v(4973.37, 947.26) * mm, v(4996.74, 1147.26) * mm, v(5011.37, 1247.26) * mm, v(5030.6, 1349.35) * mm], "startDerivative": vector(-189.04, 770.23) * mm, "endDerivative": vector(448.07, 1901.96) * mm});
            skLineSegment(sketch, "E367", {"start": v(2238.81, 1021.87) * mm, "end": v(2247.06, 1046.85) * mm});
            skLineSegment(sketch, "E368", {"start": v(2247.06, 1046.85) * mm, "end": v(2037.97, 1046.85) * mm});
            skLineSegment(sketch, "E369", {"start": v(2247.06, 1046.85) * mm, "end": v(2256.38, 1075.08) * mm});
            skFitSpline(sketch, "E370", {"points": [v(2258.48, 942.9) * mm, v(2266.12, 990.74) * mm, v(2269.2, 1016.45) * mm, v(2266.37, 1037.52) * mm, v(2259.75, 1046.85) * mm, v(2248.64, 1041.9) * mm, v(2241.7, 1029.55) * mm, v(2229.88, 994.85) * mm, v(2217.48, 942.9) * mm], "startDerivative": vector(69.99, 299.65) * mm, "endDerivative": vector(-63.8, -297.22) * mm});
            skSolve(sketch);
        }
        {
            var Q0;
            {var subQ3=sQuery(id+"F0.wireOp",EDGE,"E145");Q0=makeQuery(id+"F0.imprint","IMPRINT",FACE,{"disambiguationData":[TD([[makeQuery(id+"F0.imprint","IMPRINT",EDGE,{"derivedFrom":subQ3}),1.0]])]});}
            var Q1;
            {var subQ0=sQuery(id+"F0.wireOp",EDGE,"E95");Q1=makeQuery(id+"F0.imprint","IMPRINT",FACE,{"disambiguationData":[TD([[makeQuery(id+"F0.imprint","IMPRINT",EDGE,{"derivedFrom":subQ0}),1.0]])]});}
            var Q2;
            {var subQ1=sQuery(id+"F0.wireOp",EDGE,"E119");Q2=makeQuery(id+"F0.imprint","IMPRINT",FACE,{"disambiguationData":[TD([[makeQuery(id+"F0.imprint","IMPRINT",EDGE,{"derivedFrom":subQ1}),-1.0]])]});}
            var Q3;
            {var subQ0=sQuery(id+"F0.wireOp",EDGE,"E120");Q3=makeQuery(id+"F0.imprint","IMPRINT",FACE,{"disambiguationData":[TD([[makeQuery(id+"F0.imprint","IMPRINT",EDGE,{"derivedFrom":subQ0}),-1.0]])]});}
            var Q4;
            {var subQ3=sQuery(id+"F0.wireOp",EDGE,"E96");Q4=makeQuery(id+"F0.imprint","IMPRINT",FACE,{"disambiguationData":[TD([[makeQuery(id+"F0.imprint","IMPRINT",EDGE,{"derivedFrom":subQ3}),1.0]])]});}
            var Q5;
            {var subQ1=sQuery(id+"F0.wireOp",EDGE,"E97");Q5=makeQuery(id+"F0.imprint","IMPRINT",FACE,{"disambiguationData":[TD([[makeQuery(id+"F0.imprint","IMPRINT",EDGE,{"derivedFrom":subQ1}),1.0]])]});}
            var Q6;
            {var subQ0=sQuery(id+"F0.wireOp",EDGE,"E121");Q6=makeQuery(id+"F0.imprint","IMPRINT",FACE,{"disambiguationData":[TD([[makeQuery(id+"F0.imprint","IMPRINT",EDGE,{"derivedFrom":subQ0}),-1.0]])]});}
            var Q7;
            {var subQ0=sQuery(id+"F0.wireOp",EDGE,"E99");Q7=makeQuery(id+"F0.imprint","IMPRINT",FACE,{"disambiguationData":[TD([[makeQuery(id+"F0.imprint","IMPRINT",EDGE,{"derivedFrom":subQ0}),1.0]])]});}
            var Q8;
            {var subQ0=sQuery(id+"F0.wireOp",EDGE,"E100");Q8=makeQuery(id+"F0.imprint","IMPRINT",FACE,{"disambiguationData":[TD([[makeQuery(id+"F0.imprint","IMPRINT",EDGE,{"derivedFrom":subQ0}),1.0]])]});}
            var Q9;
            {var subQ0=sQuery(id+"F0.wireOp",EDGE,"E124");Q9=makeQuery(id+"F0.imprint","IMPRINT",FACE,{"disambiguationData":[TD([[makeQuery(id+"F0.imprint","IMPRINT",EDGE,{"derivedFrom":subQ0}),-1.0]])]});}
            var Q10;
            {var subQ2=sQuery(id+"F0.wireOp",EDGE,"E123");Q10=makeQuery(id+"F0.imprint","IMPRINT",FACE,{"disambiguationData":[TD([[makeQuery(id+"F0.imprint","IMPRINT",EDGE,{"derivedFrom":subQ2}),-1.0]])]});}
            var Q11;
            {var subQ0=sQuery(id+"F0.wireOp",EDGE,"E122");Q11=makeQuery(id+"F0.imprint","IMPRINT",FACE,{"disambiguationData":[TD([[makeQuery(id+"F0.imprint","IMPRINT",EDGE,{"derivedFrom":subQ0}),-1.0]])]});}
            var Q12;
            {var subQ0=sQuery(id+"F0.wireOp",EDGE,"E125");Q12=makeQuery(id+"F0.imprint","IMPRINT",FACE,{"disambiguationData":[TD([[makeQuery(id+"F0.imprint","IMPRINT",EDGE,{"derivedFrom":subQ0}),-1.0]])]});}
            var Q13;
            {var subQ1=sQuery(id+"F0.wireOp",EDGE,"E126");Q13=makeQuery(id+"F0.imprint","IMPRINT",FACE,{"disambiguationData":[TD([[makeQuery(id+"F0.imprint","IMPRINT",EDGE,{"derivedFrom":subQ1}),-1.0]])]});}
            var Q14;
            {var subQ0=sQuery(id+"F0.wireOp",EDGE,"E127");Q14=makeQuery(id+"F0.imprint","IMPRINT",FACE,{"disambiguationData":[TD([[makeQuery(id+"F0.imprint","IMPRINT",EDGE,{"derivedFrom":subQ0}),-1.0]])]});}
            var Q15;
            {var subQ0=sQuery(id+"F0.wireOp",EDGE,"E128");Q15=makeQuery(id+"F0.imprint","IMPRINT",FACE,{"disambiguationData":[TD([[makeQuery(id+"F0.imprint","IMPRINT",EDGE,{"derivedFrom":subQ0}),-1.0]])]});}
            var Q16;
            {var subQ0=sQuery(id+"F0.wireOp",EDGE,"E129");Q16=makeQuery(id+"F0.imprint","IMPRINT",FACE,{"disambiguationData":[TD([[makeQuery(id+"F0.imprint","IMPRINT",EDGE,{"derivedFrom":subQ0}),-1.0]])]});}
            var Q17;
            {var subQ2=sQuery(id+"F0.wireOp",EDGE,"E130");Q17=makeQuery(id+"F0.imprint","IMPRINT",FACE,{"disambiguationData":[TD([[makeQuery(id+"F0.imprint","IMPRINT",EDGE,{"derivedFrom":subQ2}),-1.0]])]});}
            var Q18;
            {var subQ0=sQuery(id+"F0.wireOp",EDGE,"E101");Q18=makeQuery(id+"F0.imprint","IMPRINT",FACE,{"disambiguationData":[TD([[makeQuery(id+"F0.imprint","IMPRINT",EDGE,{"derivedFrom":subQ0}),1.0]])]});}
            var Q19;
            {var subQ0=sQuery(id+"F0.wireOp",EDGE,"E102");Q19=makeQuery(id+"F0.imprint","IMPRINT",FACE,{"disambiguationData":[TD([[makeQuery(id+"F0.imprint","IMPRINT",EDGE,{"derivedFrom":subQ0}),1.0]])]});}
            var Q20;
            {var subQ0=sQuery(id+"F0.wireOp",EDGE,"E103");Q20=makeQuery(id+"F0.imprint","IMPRINT",FACE,{"disambiguationData":[TD([[makeQuery(id+"F0.imprint","IMPRINT",EDGE,{"derivedFrom":subQ0}),1.0]])]});}
            var Q21;
            {var subQ0=sQuery(id+"F0.wireOp",EDGE,"E104");Q21=makeQuery(id+"F0.imprint","IMPRINT",FACE,{"disambiguationData":[TD([[makeQuery(id+"F0.imprint","IMPRINT",EDGE,{"derivedFrom":subQ0}),1.0]])]});}
            var Q22;
            {var subQ0=sQuery(id+"F0.wireOp",EDGE,"E105");Q22=makeQuery(id+"F0.imprint","IMPRINT",FACE,{"disambiguationData":[TD([[makeQuery(id+"F0.imprint","IMPRINT",EDGE,{"derivedFrom":subQ0}),1.0]])]});}
            var Q23;
            {var subQ0=sQuery(id+"F0.wireOp",EDGE,"E106");Q23=makeQuery(id+"F0.imprint","IMPRINT",FACE,{"disambiguationData":[TD([[makeQuery(id+"F0.imprint","IMPRINT",EDGE,{"derivedFrom":subQ0}),1.0]])]});}
            var Q24;
            {var subQ5=sQuery(id+"F0.wireOp",EDGE,"E115");Q24=makeQuery(id+"F0.imprint","IMPRINT",FACE,{"disambiguationData":[TD([[makeQuery(id+"F0.imprint","IMPRINT",EDGE,{"derivedFrom":subQ5}),-1.0]])]});}
            var Q25;
            {var subQ5=sQuery(id+"F0.wireOp",EDGE,"E113");Q25=makeQuery(id+"F0.imprint","IMPRINT",FACE,{"disambiguationData":[TD([[makeQuery(id+"F0.imprint","IMPRINT",EDGE,{"derivedFrom":subQ5}),-1.0]])]});}
            var Q26;
            {var subQ5=sQuery(id+"F0.wireOp",EDGE,"E118");Q26=makeQuery(id+"F0.imprint","IMPRINT",FACE,{"disambiguationData":[TD([[makeQuery(id+"F0.imprint","IMPRINT",EDGE,{"derivedFrom":subQ5}),-1.0]])]});}
            var Q27;
            {var subQ5=sQuery(id+"F0.wireOp",EDGE,"E116");Q27=makeQuery(id+"F0.imprint","IMPRINT",FACE,{"disambiguationData":[TD([[makeQuery(id+"F0.imprint","IMPRINT",EDGE,{"derivedFrom":subQ5}),-1.0]])]});}
            var Q28;
            {var subQ0=sQuery(id+"F0.wireOp",EDGE,"E146");Q28=makeQuery(id+"F0.imprint","IMPRINT",FACE,{"disambiguationData":[TD([[makeQuery(id+"F0.imprint","IMPRINT",EDGE,{"derivedFrom":subQ0}),-1.0]])]});}
            var Q29;
            {var subQ0=sQuery(id+"F0.wireOp",EDGE,"E146");Q29=makeQuery(id+"F0.imprint","IMPRINT",FACE,{"disambiguationData":[TD([[makeQuery(id+"F0.imprint","IMPRINT",EDGE,{"derivedFrom":subQ0}),1.0]])]});}
            var Q30;
            {var subQ3=sQuery(id+"F0.wireOp",EDGE,"E153");Q30=makeQuery(id+"F0.imprint","IMPRINT",FACE,{"disambiguationData":[TD([[makeQuery(id+"F0.imprint","IMPRINT",EDGE,{"derivedFrom":subQ3}),1.0]])]});}
            var Q31;
            {var subQ3=sQuery(id+"F0.wireOp",EDGE,"E151");Q31=makeQuery(id+"F0.imprint","IMPRINT",FACE,{"disambiguationData":[TD([[makeQuery(id+"F0.imprint","IMPRINT",EDGE,{"derivedFrom":subQ3}),-1.0]])]});}
            var Q32;
            {var subQ0=sQuery(id+"F0.wireOp",EDGE,"E98");Q32=makeQuery(id+"F0.imprint","IMPRINT",FACE,{"disambiguationData":[TD([[makeQuery(id+"F0.imprint","IMPRINT",EDGE,{"derivedFrom":subQ0}),1.0]])]});}
            var Q33;
            {var subQ5=sQuery(id+"F0.wireOp",EDGE,"E155");Q33=makeQuery(id+"F0.imprint","IMPRINT",FACE,{"disambiguationData":[TD([[makeQuery(id+"F0.imprint","IMPRINT",EDGE,{"derivedFrom":subQ5}),-1.0]])]});}
            var Q34;
            {var subQ3=sQuery(id+"F0.wireOp",EDGE,"E156");var subQ5=sQuery(id+"F0.wireOp",EDGE,"E157");var subQ7=makeQuery(id+"F0.imprint","INTERSECT",VERTEX,{"derivedFrom":[subQ3,subQ5]});Q34=makeQuery(id+"F0.imprint","IMPRINT",FACE,{"disambiguationData":[TD([[makeQuery(id+"F0.imprint","IMPRINT",EDGE,{"disambiguationData":[TD([[subQ7,1.0]])],"derivedFrom":subQ3}),-1.0]])]});}
            var Q35;
            {var subQ3=sQuery(id+"F0.wireOp",EDGE,"E159");var subQ5=sQuery(id+"F0.wireOp",EDGE,"E158");var subQ7=makeQuery(id+"F0.imprint","INTERSECT",VERTEX,{"derivedFrom":[subQ5,subQ3]});Q35=makeQuery(id+"F0.imprint","IMPRINT",FACE,{"disambiguationData":[TD([[makeQuery(id+"F0.imprint","IMPRINT",EDGE,{"disambiguationData":[TD([[subQ7,1.0]])],"derivedFrom":subQ5}),-1.0]])]});}
            var Q36;
            {var subQ3=sQuery(id+"F0.wireOp",EDGE,"E159");var subQ5=sQuery(id+"F0.wireOp",EDGE,"E160");var subQ7=makeQuery(id+"F0.imprint","INTERSECT",VERTEX,{"derivedFrom":[subQ3,subQ5]});Q36=makeQuery(id+"F0.imprint","IMPRINT",FACE,{"disambiguationData":[TD([[makeQuery(id+"F0.imprint","IMPRINT",EDGE,{"disambiguationData":[TD([[subQ7,1.0]])],"derivedFrom":subQ3}),-1.0]])]});}
            var Q37;
            {var subQ4=sQuery(id+"F0.wireOp",EDGE,"E180");Q37=makeQuery(id+"F0.imprint","IMPRINT",FACE,{"disambiguationData":[TD([[makeQuery(id+"F0.imprint","IMPRINT",EDGE,{"derivedFrom":subQ4}),-1.0]])]});}
            var Q38;
            {var subQ5=sQuery(id+"F0.wireOp",EDGE,"E177");Q38=makeQuery(id+"F0.imprint","IMPRINT",FACE,{"disambiguationData":[TD([[makeQuery(id+"F0.imprint","IMPRINT",EDGE,{"derivedFrom":subQ5}),-1.0]])]});}
            var Q39;
            {var subQ3=sQuery(id+"F0.wireOp",EDGE,"E178");var subQ5=sQuery(id+"F0.wireOp",EDGE,"E179");var subQ7=makeQuery(id+"F0.imprint","INTERSECT",VERTEX,{"derivedFrom":[subQ3,subQ5]});Q39=makeQuery(id+"F0.imprint","IMPRINT",FACE,{"disambiguationData":[TD([[makeQuery(id+"F0.imprint","IMPRINT",EDGE,{"disambiguationData":[TD([[subQ7,1.0]])],"derivedFrom":subQ3}),-1.0]])]});}
            var Q40;
            {var subQ5=sQuery(id+"F0.wireOp",EDGE,"E174");Q40=makeQuery(id+"F0.imprint","IMPRINT",FACE,{"disambiguationData":[TD([[makeQuery(id+"F0.imprint","IMPRINT",EDGE,{"derivedFrom":subQ5}),-1.0]])]});}
            var Q41;
            {var subQ3=sQuery(id+"F0.wireOp",EDGE,"E175");var subQ5=sQuery(id+"F0.wireOp",EDGE,"E176");var subQ7=makeQuery(id+"F0.imprint","INTERSECT",VERTEX,{"derivedFrom":[subQ3,subQ5]});Q41=makeQuery(id+"F0.imprint","IMPRINT",FACE,{"disambiguationData":[TD([[makeQuery(id+"F0.imprint","IMPRINT",EDGE,{"disambiguationData":[TD([[subQ7,1.0]])],"derivedFrom":subQ3}),-1.0]])]});}
            var Q42;
            {var subQ5=sQuery(id+"F0.wireOp",EDGE,"E171");Q42=makeQuery(id+"F0.imprint","IMPRINT",FACE,{"disambiguationData":[TD([[makeQuery(id+"F0.imprint","IMPRINT",EDGE,{"derivedFrom":subQ5}),-1.0]])]});}
            var Q43;
            {var subQ3=sQuery(id+"F0.wireOp",EDGE,"E172");var subQ5=sQuery(id+"F0.wireOp",EDGE,"E173");var subQ6=makeQuery(id+"F0.imprint","INTERSECT",VERTEX,{"derivedFrom":[subQ3,subQ5]});Q43=makeQuery(id+"F0.imprint","IMPRINT",FACE,{"disambiguationData":[TD([[makeQuery(id+"F0.imprint","IMPRINT",EDGE,{"disambiguationData":[TD([[subQ6,1.0]])],"derivedFrom":subQ3}),-1.0]])]});}
            var Q44;
            {var subQ5=sQuery(id+"F0.wireOp",EDGE,"E167");Q44=makeQuery(id+"F0.imprint","IMPRINT",FACE,{"disambiguationData":[TD([[makeQuery(id+"F0.imprint","IMPRINT",EDGE,{"derivedFrom":subQ5}),-1.0]])]});}
            var Q45;
            {var subQ3=sQuery(id+"F0.wireOp",EDGE,"E168");var subQ5=sQuery(id+"F0.wireOp",EDGE,"E169");var subQ6=makeQuery(id+"F0.imprint","INTERSECT",VERTEX,{"derivedFrom":[subQ3,subQ5]});Q45=makeQuery(id+"F0.imprint","IMPRINT",FACE,{"disambiguationData":[TD([[makeQuery(id+"F0.imprint","IMPRINT",EDGE,{"disambiguationData":[TD([[subQ6,1.0]])],"derivedFrom":subQ3}),-1.0]])]});}
            var Q46;
            {var subQ5=sQuery(id+"F0.wireOp",EDGE,"E164");Q46=makeQuery(id+"F0.imprint","IMPRINT",FACE,{"disambiguationData":[TD([[makeQuery(id+"F0.imprint","IMPRINT",EDGE,{"derivedFrom":subQ5}),1.0]])]});}
            var Q47;
            {var subQ5=sQuery(id+"F0.wireOp",EDGE,"E163");Q47=makeQuery(id+"F0.imprint","IMPRINT",FACE,{"disambiguationData":[TD([[makeQuery(id+"F0.imprint","IMPRINT",EDGE,{"derivedFrom":subQ5}),1.0]])]});}
            var Q48;
            {var subQ5=sQuery(id+"F0.wireOp",EDGE,"E161");Q48=makeQuery(id+"F0.imprint","IMPRINT",FACE,{"disambiguationData":[TD([[makeQuery(id+"F0.imprint","IMPRINT",EDGE,{"derivedFrom":subQ5}),1.0]])]});}
            var Q49;
            {var subQ1=sQuery(id+"F0.wireOp",EDGE,"E95");Q49=makeQuery(id+"F0.imprint","IMPRINT",FACE,{"disambiguationData":[TD([[makeQuery(id+"F0.imprint","IMPRINT",EDGE,{"derivedFrom":subQ1}),-1.0]])]});}
            var Q50;
            {var subQ0=sQuery(id+"F0.wireOp",EDGE,"E119");Q50=makeQuery(id+"F0.imprint","IMPRINT",FACE,{"disambiguationData":[TD([[makeQuery(id+"F0.imprint","IMPRINT",EDGE,{"derivedFrom":subQ0}),1.0]])]});}
            extrude(context, id + "F1", {"entities" : qUnion([Q0, Q1, Q2, Q3, Q4, Q5, Q6, Q7, Q8, Q9, Q10, Q11, Q12, Q13, Q14, Q15, Q16, Q17, Q18, Q19, Q20, Q21, Q22, Q23, Q24, Q25, Q26, Q27, Q28, Q29, Q30, Q31, Q32, Q33, Q34, Q35, Q36, Q37, Q38, Q39, Q40, Q41, Q42, Q43, Q44, Q45, Q46, Q47, Q48, Q49, Q50]), "depth" : 15 * mm});
        }
        {
            var Q0;
            Q0=qCreatedBy(makeId("Front.planeOp"),FACE);
            var sketch = newSketch(context, id + "F2", { "sketchPlane" : qUnion([Q0])});
            skPoint(sketch, "E371", {"position": v(1164.9, -1155.23) * mm});
            skPoint(sketch, "E372", {"position": v(1152.1, -1055.23) * mm});
            skPoint(sketch, "E373", {"position": v(1137.89, -855.23) * mm});
            skPoint(sketch, "E374", {"position": v(1129.18, -655.23) * mm});
            skPoint(sketch, "E375", {"position": v(1117.43, -455.23) * mm});
            skPoint(sketch, "E376", {"position": v(1114.05, -255.23) * mm});
            skPoint(sketch, "E377", {"position": v(1116.93, -55.23) * mm});
            skPoint(sketch, "E378", {"position": v(1117.9, 144.77) * mm});
            skPoint(sketch, "E379", {"position": v(1123.27, 344.77) * mm});
            skPoint(sketch, "E380", {"position": v(1136.96, 544.77) * mm});
            skPoint(sketch, "E381", {"position": v(1157.2, 744.77) * mm});
            skPoint(sketch, "E382", {"position": v(1241.41, 944.77) * mm});
            skPoint(sketch, "E383", {"position": v(1187.05, 944.77) * mm});
            skPoint(sketch, "E384", {"position": v(1253.71, 1044.77) * mm});
            skPoint(sketch, "E385", {"position": v(1206.98, 1044.77) * mm});
            skPoint(sketch, "E386", {"position": v(1207.01, 1044.77) * mm});
            skLineSegment(sketch, "E387", {"start": v(1253.71, 1044.77) * mm, "end": v(1206.98, 1044.77) * mm});
            skLineSegment(sketch, "E388", {"start": v(1241.41, 944.77) * mm, "end": v(1187.05, 944.77) * mm});
            skLineSegment(sketch, "E389", {"start": v(1214.23, 944.77) * mm, "end": v(1241.41, 944.77) * mm});
            skLineSegment(sketch, "E390", {"start": v(1220.51, 744.77) * mm, "end": v(1157.2, 744.77) * mm});
            skLineSegment(sketch, "E391", {"start": v(1210.37, 544.77) * mm, "end": v(1136.96, 544.77) * mm});
            skLineSegment(sketch, "E392", {"start": v(1203.3, 344.77) * mm, "end": v(1123.27, 344.77) * mm});
            skLineSegment(sketch, "E393", {"start": v(1200.72, 144.77) * mm, "end": v(1117.9, 144.77) * mm});
            skLineSegment(sketch, "E394", {"start": v(1200.75, -55.23) * mm, "end": v(1116.93, -55.23) * mm});
            skLineSegment(sketch, "E395", {"start": v(1200.32, -255.23) * mm, "end": v(1114.05, -255.23) * mm});
            skLineSegment(sketch, "E396", {"start": v(1199.61, -455.23) * mm, "end": v(1117.43, -455.23) * mm});
            skLineSegment(sketch, "E397", {"start": v(1201.9, -655.23) * mm, "end": v(1129.18, -655.23) * mm});
            skLineSegment(sketch, "E398", {"start": v(1204.76, -855.23) * mm, "end": v(1137.89, -855.23) * mm});
            skLineSegment(sketch, "E399", {"start": v(1207.57, -1055.23) * mm, "end": v(1152.1, -1055.23) * mm});
            skLineSegment(sketch, "E400", {"start": v(1208.69, -1155.23) * mm, "end": v(1164.9, -1155.23) * mm});
            skLineSegment(sketch, "E401", {"start": v(1206.98, 1044.77) * mm, "end": v(1211.36, 1044.77) * mm});
            skLineSegment(sketch, "E402", {"start": v(1211.36, 1044.77) * mm, "end": v(1252.36, 1044.77) * mm});
            skLineSegment(sketch, "E403", {"start": v(1252.36, 1044.77) * mm, "end": v(1253.71, 1044.77) * mm});
            skLineSegment(sketch, "E404", {"start": v(1253.64, 1148.73) * mm, "end": v(1253.64, 1179.6) * mm});
            skLineSegment(sketch, "E405", {"start": v(1267.59, 1136.52) * mm, "end": v(1267.59, 1183.24) * mm});
            skLineSegment(sketch, "E406", {"start": v(1187.05, 944.77) * mm, "end": v(1192.73, 944.77) * mm});
            skLineSegment(sketch, "E407", {"start": v(1192.73, 944.77) * mm, "end": v(1237.73, 944.77) * mm});
            skLineSegment(sketch, "E408", {"start": v(1237.73, 944.77) * mm, "end": v(1241.41, 944.77) * mm});
            skLineSegment(sketch, "E409", {"start": v(1220.51, 744.77) * mm, "end": v(1214.36, 744.77) * mm});
            skLineSegment(sketch, "E410", {"start": v(1214.36, 744.77) * mm, "end": v(1163.36, 744.77) * mm});
            skLineSegment(sketch, "E411", {"start": v(1163.36, 744.77) * mm, "end": v(1157.2, 744.77) * mm});
            skLineSegment(sketch, "E412", {"start": v(1203.17, 544.77) * mm, "end": v(1144.16, 544.77) * mm});
            skLineSegment(sketch, "E413", {"start": v(1144.16, 544.77) * mm, "end": v(1136.96, 544.77) * mm});
            skLineSegment(sketch, "E414", {"start": v(1195.8, 344.77) * mm, "end": v(1130.77, 344.77) * mm});
            skLineSegment(sketch, "E415", {"start": v(1130.77, 344.77) * mm, "end": v(1123.27, 344.77) * mm});
            skLineSegment(sketch, "E416", {"start": v(1193.32, 144.77) * mm, "end": v(1125.3, 144.77) * mm});
            skLineSegment(sketch, "E417", {"start": v(1125.3, 144.77) * mm, "end": v(1117.9, 144.77) * mm});
            skLineSegment(sketch, "E418", {"start": v(1193.04, -55.23) * mm, "end": v(1124.64, -55.23) * mm});
            skLineSegment(sketch, "E419", {"start": v(1124.64, -55.23) * mm, "end": v(1116.93, -55.23) * mm});
            skLineSegment(sketch, "E420", {"start": v(1192.2, -255.23) * mm, "end": v(1122.18, -255.23) * mm});
            skLineSegment(sketch, "E421", {"start": v(1122.18, -255.23) * mm, "end": v(1114.05, -255.23) * mm});
            skLineSegment(sketch, "E422", {"start": v(1192.02, -455.23) * mm, "end": v(1125.02, -455.23) * mm});
            skLineSegment(sketch, "E423", {"start": v(1125.02, -455.23) * mm, "end": v(1117.43, -455.23) * mm});
            skLineSegment(sketch, "E424", {"start": v(1195.24, -655.23) * mm, "end": v(1135.84, -655.23) * mm});
            skLineSegment(sketch, "E425", {"start": v(1135.84, -655.23) * mm, "end": v(1129.18, -655.23) * mm});
            skLineSegment(sketch, "E426", {"start": v(1198.32, -855.23) * mm, "end": v(1144.33, -855.23) * mm});
            skLineSegment(sketch, "E427", {"start": v(1144.33, -855.23) * mm, "end": v(1137.89, -855.23) * mm});
            skLineSegment(sketch, "E428", {"start": v(1202.23, -1055.23) * mm, "end": v(1157.45, -1055.23) * mm});
            skLineSegment(sketch, "E429", {"start": v(1157.45, -1055.23) * mm, "end": v(1152.1, -1055.23) * mm});
            skLineSegment(sketch, "E430", {"start": v(1204.6, -1155.23) * mm, "end": v(1169, -1155.23) * mm});
            skLineSegment(sketch, "E431", {"start": v(1169, -1155.23) * mm, "end": v(1164.9, -1155.23) * mm});
            skFitSpline(sketch, "E432", {"points": [v(1252.36, 1044.77) * mm, v(1237.73, 944.77) * mm, v(1214.36, 744.77) * mm, v(1203.17, 544.77) * mm, v(1195.8, 344.77) * mm, v(1193.32, 144.77) * mm, v(1193.04, -55.23) * mm, v(1192.2, -255.23) * mm, v(1192.02, -455.23) * mm, v(1195.24, -655.23) * mm, v(1198.32, -855.23) * mm, v(1202.23, -1055.23) * mm, v(1204.6, -1155.23) * mm], "startDerivative": vector(-207.13, -1457.4) * mm, "endDerivative": vector(36.18, -1464.69) * mm});
            skFitSpline(sketch, "E433", {"points": [v(1211.36, 1044.77) * mm, v(1192.73, 944.77) * mm, v(1163.36, 744.77) * mm, v(1144.16, 544.77) * mm, v(1130.77, 344.77) * mm, v(1125.3, 144.77) * mm, v(1124.64, -55.23) * mm, v(1122.18, -255.23) * mm, v(1125.02, -455.23) * mm, v(1135.84, -655.23) * mm, v(1144.33, -855.23) * mm, v(1157.45, -1055.23) * mm, v(1169, -1155.23) * mm], "startDerivative": vector(-284.6, -1452.48) * mm, "endDerivative": vector(190.25, -1460.4) * mm});
            skLineSegment(sketch, "E434", {"start": v(1252.36, 1044.77) * mm, "end": v(1231.86, 1044.77) * mm});
            skLineSegment(sketch, "E435", {"start": v(1125.3, 144.77) * mm, "end": v(1031.86, 144.77) * mm});
            skLineSegment(sketch, "E436", {"start": v(1031.86, 144.77) * mm, "end": v(1031.86, -1518.16) * mm});
            skLineSegment(sketch, "E437", {"start": v(1031.86, 144.77) * mm, "end": v(1031.86, 1298.18) * mm});
            skLineSegment(sketch, "E438", {"start": v(1211.36, 1044.77) * mm, "end": v(1031.86, 1044.77) * mm});
            skLineSegment(sketch, "E439", {"start": v(1192.73, 944.77) * mm, "end": v(1031.86, 944.77) * mm});
            skLineSegment(sketch, "E440", {"start": v(1163.36, 744.77) * mm, "end": v(1031.86, 744.77) * mm});
            skLineSegment(sketch, "E441", {"start": v(1144.16, 544.77) * mm, "end": v(1031.86, 544.77) * mm});
            skLineSegment(sketch, "E442", {"start": v(1130.77, 344.77) * mm, "end": v(1031.86, 344.77) * mm});
            skLineSegment(sketch, "E443", {"start": v(1124.64, -55.23) * mm, "end": v(1031.86, -55.23) * mm});
            skLineSegment(sketch, "E444", {"start": v(1122.18, -255.23) * mm, "end": v(1031.86, -255.23) * mm});
            skLineSegment(sketch, "E445", {"start": v(1125.02, -455.23) * mm, "end": v(1031.86, -455.23) * mm});
            skLineSegment(sketch, "E446", {"start": v(1135.84, -655.23) * mm, "end": v(1031.86, -655.23) * mm});
            skLineSegment(sketch, "E447", {"start": v(1144.33, -855.23) * mm, "end": v(1031.86, -855.23) * mm});
            skLineSegment(sketch, "E448", {"start": v(1157.45, -1055.23) * mm, "end": v(1031.86, -1055.23) * mm});
            skLineSegment(sketch, "E449", {"start": v(1169, -1155.23) * mm, "end": v(1031.86, -1155.23) * mm});
            skLineSegment(sketch, "E450", {"start": v(1195.83, -1259.19) * mm, "end": v(1031.86, -1259.19) * mm});
            skLineSegment(sketch, "E451", {"start": v(1031.86, -1155.23) * mm, "end": v(1031.86, -1180.23) * mm});
            skLineSegment(sketch, "E452", {"start": v(1031.86, -1180.23) * mm, "end": v(1031.86, -1209.19) * mm});
            skLineSegment(sketch, "E453", {"start": v(1031.86, -1209.19) * mm, "end": v(1031.86, -1234.19) * mm});
            skLineSegment(sketch, "E454", {"start": v(1031.86, -1234.19) * mm, "end": v(1031.86, -1259.19) * mm});
            skLineSegment(sketch, "E455", {"start": v(1031.86, -1234.19) * mm, "end": v(1180.42, -1234.19) * mm});
            skLineSegment(sketch, "E456", {"start": v(1209.3, -1233.64) * mm, "end": v(1180.42, -1234.19) * mm});
            skLineSegment(sketch, "E457", {"start": v(1253.64, 1148.73) * mm, "end": v(1031.86, 1148.73) * mm});
            skLineSegment(sketch, "E458", {"start": v(1031.86, 1148.73) * mm, "end": v(1031.86, 1123.75) * mm});
            skLineSegment(sketch, "E459", {"start": v(1031.86, 1123.75) * mm, "end": v(1232.7, 1123.75) * mm});
            skLineSegment(sketch, "E460", {"start": v(1122.18, -255.23) * mm, "end": v(1122.18, 1148.73) * mm});
            skLineSegment(sketch, "E461", {"start": v(1122.18, -255.23) * mm, "end": v(1122.18, -1259.19) * mm});
            skLineSegment(sketch, "E462", {"start": v(1122.18, -1259.19) * mm, "end": v(1122.18, 1148.73) * mm});
            skLineSegment(sketch, "E463", {"start": v(1252.36, 1044.77) * mm, "end": v(1237.36, 1044.77) * mm});
            skLineSegment(sketch, "E464", {"start": v(1237.73, 944.77) * mm, "end": v(1222.73, 944.77) * mm});
            skLineSegment(sketch, "E465", {"start": v(1214.36, 744.77) * mm, "end": v(1199.36, 744.77) * mm});
            skLineSegment(sketch, "E466", {"start": v(1203.17, 544.77) * mm, "end": v(1188.17, 544.77) * mm});
            skLineSegment(sketch, "E467", {"start": v(1195.8, 344.77) * mm, "end": v(1180.8, 344.77) * mm});
            skLineSegment(sketch, "E468", {"start": v(1193.32, 144.77) * mm, "end": v(1178.32, 144.77) * mm});
            skLineSegment(sketch, "E469", {"start": v(1193.04, -55.23) * mm, "end": v(1178.04, -55.23) * mm});
            skLineSegment(sketch, "E470", {"start": v(1192.2, -255.23) * mm, "end": v(1177.2, -255.23) * mm});
            skLineSegment(sketch, "E471", {"start": v(1192.02, -455.23) * mm, "end": v(1177.02, -455.23) * mm});
            skLineSegment(sketch, "E472", {"start": v(1195.24, -655.23) * mm, "end": v(1180.24, -655.23) * mm});
            skLineSegment(sketch, "E473", {"start": v(1198.32, -855.23) * mm, "end": v(1183.32, -855.23) * mm});
            skLineSegment(sketch, "E474", {"start": v(1202.23, -1055.23) * mm, "end": v(1187.23, -1055.23) * mm});
            skLineSegment(sketch, "E475", {"start": v(1204.6, -1155.23) * mm, "end": v(1189.6, -1155.23) * mm});
            skLineSegment(sketch, "E476", {"start": v(1194.3, -1233.93) * mm, "end": v(1209.3, -1233.64) * mm});
            skLineSegment(sketch, "E477", {"start": v(1252.49, 1045.32) * mm, "end": v(1252.77, 1045.32) * mm});
            skLineSegment(sketch, "E478", {"start": v(1252.77, 1045.32) * mm, "end": v(1252.77, 1043.6) * mm});
            skLineSegment(sketch, "E479", {"start": v(1252.77, 1043.6) * mm, "end": v(1252.2, 1043.6) * mm});
            skLineSegment(sketch, "E480", {"start": v(1237.85, 945.61) * mm, "end": v(1238.08, 945.61) * mm});
            skLineSegment(sketch, "E481", {"start": v(1238.08, 945.61) * mm, "end": v(1238.08, 943.7) * mm});
            skLineSegment(sketch, "E482", {"start": v(1238.08, 943.7) * mm, "end": v(1237.58, 943.7) * mm});
            skLineSegment(sketch, "E483", {"start": v(1214.44, 745.62) * mm, "end": v(1214.83, 745.62) * mm});
            skLineSegment(sketch, "E484", {"start": v(1214.83, 745.62) * mm, "end": v(1214.83, 743.53) * mm});
            skLineSegment(sketch, "E485", {"start": v(1214.83, 743.53) * mm, "end": v(1214.26, 743.53) * mm});
            skLineSegment(sketch, "E486", {"start": v(1211.36, 1044.77) * mm, "end": v(1226.36, 1044.77) * mm});
            skLineSegment(sketch, "E487", {"start": v(1192.73, 944.77) * mm, "end": v(1207.73, 944.77) * mm});
            skLineSegment(sketch, "E488", {"start": v(1163.36, 744.77) * mm, "end": v(1178.36, 744.77) * mm});
            skLineSegment(sketch, "E489", {"start": v(1144.16, 544.77) * mm, "end": v(1159.16, 544.77) * mm});
            skLineSegment(sketch, "E490", {"start": v(1130.77, 344.77) * mm, "end": v(1145.77, 344.77) * mm});
            skLineSegment(sketch, "E491", {"start": v(1125.3, 144.77) * mm, "end": v(1140.3, 144.77) * mm});
            skLineSegment(sketch, "E492", {"start": v(1124.64, -55.23) * mm, "end": v(1139.64, -55.23) * mm});
            skLineSegment(sketch, "E493", {"start": v(1122.18, -255.23) * mm, "end": v(1137.18, -255.23) * mm});
            skLineSegment(sketch, "E494", {"start": v(1125.02, -455.23) * mm, "end": v(1140.02, -455.23) * mm});
            skLineSegment(sketch, "E495", {"start": v(1135.84, -655.23) * mm, "end": v(1150.84, -655.23) * mm});
            skLineSegment(sketch, "E496", {"start": v(1144.33, -855.23) * mm, "end": v(1159.33, -855.23) * mm});
            skLineSegment(sketch, "E497", {"start": v(1157.45, -1055.23) * mm, "end": v(1172.45, -1055.23) * mm});
            skLineSegment(sketch, "E498", {"start": v(1169, -1155.23) * mm, "end": v(1184, -1155.23) * mm});
            skLineSegment(sketch, "E499", {"start": v(1180.42, -1234.19) * mm, "end": v(1195.42, -1233.9) * mm});
            skLineSegment(sketch, "E500", {"start": v(1211.55, 1045.65) * mm, "end": v(1210.55, 1045.65) * mm});
            skLineSegment(sketch, "E501", {"start": v(1210.55, 1045.65) * mm, "end": v(1210.55, 1043.51) * mm});
            skLineSegment(sketch, "E502", {"start": v(1210.55, 1043.51) * mm, "end": v(1211.12, 1043.51) * mm});
            skLineSegment(sketch, "E503", {"start": v(1237.32, 1044.78) * mm, "end": v(1237.3, 1044.78) * mm});
            skLineSegment(sketch, "E504", {"start": v(1237.3, 1044.78) * mm, "end": v(1237.3, 1044.76) * mm});
            skLineSegment(sketch, "E505", {"start": v(1237.3, 1044.76) * mm, "end": v(1237.32, 1044.76) * mm});
            skLineSegment(sketch, "E506", {"start": v(1237.36, 1044.77) * mm, "end": v(1237.36, 1044.8) * mm});
            skLineSegment(sketch, "E507", {"start": v(1237.36, 1044.8) * mm, "end": v(1237.34, 1044.8) * mm});
            skLineSegment(sketch, "E508", {"start": v(1237.34, 1044.8) * mm, "end": v(1237.34, 1044.74) * mm});
            skLineSegment(sketch, "E509", {"start": v(1237.34, 1044.74) * mm, "end": v(1237.36, 1044.74) * mm});
            skLineSegment(sketch, "E510", {"start": v(1237.36, 1044.74) * mm, "end": v(1237.36, 1044.77) * mm});
            skLineSegment(sketch, "E511", {"start": v(1256.33, 1146.02) * mm, "end": v(1256.38, 1145.94) * mm});
            skLineSegment(sketch, "E512", {"start": v(1203.17, 544.77) * mm, "end": v(1203.27, 544.77) * mm});
            skLineSegment(sketch, "E513", {"start": v(1203.27, 544.77) * mm, "end": v(1203.27, 544.51) * mm});
            skLineSegment(sketch, "E514", {"start": v(1203.27, 544.51) * mm, "end": v(1203.16, 544.51) * mm});
            skLineSegment(sketch, "E515", {"start": v(1203.27, 544.77) * mm, "end": v(1203.27, 544.98) * mm});
            skLineSegment(sketch, "E516", {"start": v(1203.27, 544.98) * mm, "end": v(1203.17, 544.98) * mm});
            skLineSegment(sketch, "E517", {"start": v(1196.73, 344.77) * mm, "end": v(1196.73, 344.07) * mm});
            skLineSegment(sketch, "E518", {"start": v(1196.73, 344.07) * mm, "end": v(1195.58, 344.07) * mm});
            skLineSegment(sketch, "E519", {"start": v(1196.73, 344.77) * mm, "end": v(1196.73, 345.42) * mm});
            skLineSegment(sketch, "E520", {"start": v(1196.73, 345.42) * mm, "end": v(1195.5, 345.42) * mm});
            skLineSegment(sketch, "E521", {"start": v(1193.32, 146.03) * mm, "end": v(1194.57, 146.03) * mm});
            skLineSegment(sketch, "E522", {"start": v(1194.57, 146.03) * mm, "end": v(1194.57, 143.45) * mm});
            skLineSegment(sketch, "E523", {"start": v(1194.57, 143.45) * mm, "end": v(1191.82, 143.45) * mm});
            skLineSegment(sketch, "E524", {"start": v(1192.44, -54.7) * mm, "end": v(1193.38, -54.7) * mm});
            skLineSegment(sketch, "E525", {"start": v(1193.38, -54.7) * mm, "end": v(1193.38, -55.72) * mm});
            skLineSegment(sketch, "E526", {"start": v(1193.38, -55.72) * mm, "end": v(1192.2, -55.72) * mm});
            skLineSegment(sketch, "E527", {"start": v(1192.2, -255.54) * mm, "end": v(1192.56, -255.54) * mm});
            skLineSegment(sketch, "E528", {"start": v(1192.56, -255.54) * mm, "end": v(1192.6, -254.61) * mm});
            skLineSegment(sketch, "E529", {"start": v(1192.6, -254.61) * mm, "end": v(1192.2, -254.63) * mm});
            skLineSegment(sketch, "E530", {"start": v(1192.03, -456.16) * mm, "end": v(1193.05, -456.16) * mm});
            skLineSegment(sketch, "E531", {"start": v(1193.05, -456.16) * mm, "end": v(1193.05, -453.09) * mm});
            skLineSegment(sketch, "E532", {"start": v(1193.05, -453.09) * mm, "end": v(1192.02, -453.09) * mm});
            skLineSegment(sketch, "E533", {"start": v(1195.23, -654.5) * mm, "end": v(1195.69, -654.5) * mm});
            skLineSegment(sketch, "E534", {"start": v(1195.69, -654.5) * mm, "end": v(1195.69, -656.59) * mm});
            skLineSegment(sketch, "E535", {"start": v(1195.69, -656.59) * mm, "end": v(1194.56, -656.63) * mm});
            skLineSegment(sketch, "E536", {"start": v(1195.23, -654.5) * mm, "end": v(1195.07, -654.5) * mm});
            skLineSegment(sketch, "E537", {"start": v(1198.3, -854.18) * mm, "end": v(1198.9, -854.18) * mm});
            skLineSegment(sketch, "E538", {"start": v(1198.9, -854.18) * mm, "end": v(1198.9, -857) * mm});
            skLineSegment(sketch, "E539", {"start": v(1198.9, -857) * mm, "end": v(1197.74, -857.06) * mm});
            skLineSegment(sketch, "E540", {"start": v(1202.2, -1053.8) * mm, "end": v(1203.22, -1053.8) * mm});
            skLineSegment(sketch, "E541", {"start": v(1203.22, -1053.8) * mm, "end": v(1203.22, -1057.36) * mm});
            skLineSegment(sketch, "E542", {"start": v(1203.22, -1057.36) * mm, "end": v(1201.35, -1057.36) * mm});
            skLineSegment(sketch, "E543", {"start": v(1204.58, -1154.31) * mm, "end": v(1205.21, -1154.31) * mm});
            skLineSegment(sketch, "E544", {"start": v(1205.21, -1154.31) * mm, "end": v(1205.22, -1156.3) * mm});
            skLineSegment(sketch, "E545", {"start": v(1205.22, -1156.3) * mm, "end": v(1204.32, -1156.36) * mm});
            skLineSegment(sketch, "E546", {"start": v(1209.29, -1233.07) * mm, "end": v(1209.81, -1233.07) * mm});
            skLineSegment(sketch, "E547", {"start": v(1209.81, -1233.07) * mm, "end": v(1209.75, -1234.05) * mm});
            skLineSegment(sketch, "E548", {"start": v(1209.75, -1234.05) * mm, "end": v(1209.07, -1234.18) * mm});
            skFitSpline(sketch, "E549", {"points": [v(1199.05, -1258.51) * mm, v(1195.42, -1233.9) * mm, v(1184, -1155.23) * mm, v(1172.45, -1055.23) * mm, v(1159.33, -855.23) * mm, v(1150.84, -655.23) * mm, v(1140.02, -455.23) * mm, v(1137.18, -255.23) * mm, v(1139.64, -55.23) * mm, v(1140.3, 144.77) * mm, v(1145.77, 344.77) * mm, v(1159.16, 544.77) * mm, v(1178.36, 744.77) * mm, v(1207.73, 944.77) * mm, v(1226.36, 1044.77) * mm, v(1256.6, 1146.87) * mm], "startDerivative": vector(-114.37, 778.22) * mm, "endDerivative": vector(603.08, 1884.97) * mm});
            skFitSpline(sketch, "E550", {"points": [v(1199.05, -1258.51) * mm, v(1194.3, -1233.93) * mm, v(1189.6, -1155.23) * mm, v(1187.23, -1055.23) * mm, v(1183.32, -855.23) * mm, v(1180.24, -655.23) * mm, v(1177.02, -455.23) * mm, v(1177.2, -255.23) * mm, v(1178.04, -55.23) * mm, v(1178.32, 144.77) * mm, v(1180.8, 344.77) * mm, v(1188.17, 544.77) * mm, v(1199.36, 744.77) * mm, v(1222.73, 944.77) * mm, v(1237.36, 1044.77) * mm, v(1256.6, 1146.87) * mm], "startDerivative": vector(-189.04, 770.23) * mm, "endDerivative": vector(448.07, 1901.96) * mm});
            skSolve(sketch);
        }
        {
            var Q0;
            {var subQ5=sQuery(id+"F2.wireOp",EDGE,"E530");Q0=makeQuery(id+"F2.imprint","IMPRINT",FACE,{"disambiguationData":[TD([[makeQuery(id+"F2.imprint","IMPRINT",EDGE,{"derivedFrom":subQ5}),1.0]])]});}
            var Q1;
            {var subQ5=sQuery(id+"F2.wireOp",EDGE,"E543");Q1=makeQuery(id+"F2.imprint","IMPRINT",FACE,{"disambiguationData":[TD([[makeQuery(id+"F2.imprint","IMPRINT",EDGE,{"derivedFrom":subQ5}),-1.0]])]});}
            var Q2;
            {var subQ5=sQuery(id+"F2.wireOp",EDGE,"E479");Q2=makeQuery(id+"F2.imprint","IMPRINT",FACE,{"disambiguationData":[TD([[makeQuery(id+"F2.imprint","IMPRINT",EDGE,{"derivedFrom":subQ5}),-1.0]])]});}
            var Q3;
            {var subQ0=sQuery(id+"F2.wireOp",EDGE,"E506");Q3=makeQuery(id+"F2.imprint","IMPRINT",FACE,{"disambiguationData":[TD([[makeQuery(id+"F2.imprint","IMPRINT",EDGE,{"derivedFrom":subQ0}),1.0]])]});}
            var Q4;
            {var subQ3=sQuery(id+"F2.wireOp",EDGE,"E519");Q4=makeQuery(id+"F2.imprint","IMPRINT",FACE,{"disambiguationData":[TD([[makeQuery(id+"F2.imprint","IMPRINT",EDGE,{"derivedFrom":subQ3}),1.0]])]});}
            var Q5;
            {var subQ3=sQuery(id+"F2.wireOp",EDGE,"E517");Q5=makeQuery(id+"F2.imprint","IMPRINT",FACE,{"disambiguationData":[TD([[makeQuery(id+"F2.imprint","IMPRINT",EDGE,{"derivedFrom":subQ3}),-1.0]])]});}
            var Q6;
            {var subQ5=sQuery(id+"F2.wireOp",EDGE,"E521");Q6=makeQuery(id+"F2.imprint","IMPRINT",FACE,{"disambiguationData":[TD([[makeQuery(id+"F2.imprint","IMPRINT",EDGE,{"derivedFrom":subQ5}),-1.0]])]});}
            var Q7;
            {var subQ3=sQuery(id+"F2.wireOp",EDGE,"E522");var subQ5=sQuery(id+"F2.wireOp",EDGE,"E523");var subQ7=makeQuery(id+"F2.imprint","INTERSECT",VERTEX,{"derivedFrom":[subQ3,subQ5]});Q7=makeQuery(id+"F2.imprint","IMPRINT",FACE,{"disambiguationData":[TD([[makeQuery(id+"F2.imprint","IMPRINT",EDGE,{"disambiguationData":[TD([[subQ7,1.0]])],"derivedFrom":subQ3}),-1.0]])]});}
            var Q8;
            {var subQ3=sQuery(id+"F2.wireOp",EDGE,"E525");var subQ5=sQuery(id+"F2.wireOp",EDGE,"E524");var subQ6=makeQuery(id+"F2.imprint","INTERSECT",VERTEX,{"derivedFrom":[subQ5,subQ3]});Q8=makeQuery(id+"F2.imprint","IMPRINT",FACE,{"disambiguationData":[TD([[makeQuery(id+"F2.imprint","IMPRINT",EDGE,{"disambiguationData":[TD([[subQ6,1.0]])],"derivedFrom":subQ5}),-1.0]])]});}
            var Q9;
            {var subQ3=sQuery(id+"F2.wireOp",EDGE,"E525");var subQ5=sQuery(id+"F2.wireOp",EDGE,"E526");var subQ7=makeQuery(id+"F2.imprint","INTERSECT",VERTEX,{"derivedFrom":[subQ3,subQ5]});Q9=makeQuery(id+"F2.imprint","IMPRINT",FACE,{"disambiguationData":[TD([[makeQuery(id+"F2.imprint","IMPRINT",EDGE,{"disambiguationData":[TD([[subQ7,1.0]])],"derivedFrom":subQ3}),-1.0]])]});}
            var Q10;
            {var subQ5=sQuery(id+"F2.wireOp",EDGE,"E529");Q10=makeQuery(id+"F2.imprint","IMPRINT",FACE,{"disambiguationData":[TD([[makeQuery(id+"F2.imprint","IMPRINT",EDGE,{"derivedFrom":subQ5}),1.0]])]});}
            var Q11;
            {var subQ5=sQuery(id+"F2.wireOp",EDGE,"E527");Q11=makeQuery(id+"F2.imprint","IMPRINT",FACE,{"disambiguationData":[TD([[makeQuery(id+"F2.imprint","IMPRINT",EDGE,{"derivedFrom":subQ5}),1.0]])]});}
            var Q12;
            {var subQ5=sQuery(id+"F2.wireOp",EDGE,"E533");Q12=makeQuery(id+"F2.imprint","IMPRINT",FACE,{"disambiguationData":[TD([[makeQuery(id+"F2.imprint","IMPRINT",EDGE,{"derivedFrom":subQ5}),-1.0]])]});}
            var Q13;
            {var subQ3=sQuery(id+"F2.wireOp",EDGE,"E534");var subQ5=sQuery(id+"F2.wireOp",EDGE,"E535");var subQ7=makeQuery(id+"F2.imprint","INTERSECT",VERTEX,{"derivedFrom":[subQ3,subQ5]});Q13=makeQuery(id+"F2.imprint","IMPRINT",FACE,{"disambiguationData":[TD([[makeQuery(id+"F2.imprint","IMPRINT",EDGE,{"disambiguationData":[TD([[subQ7,1.0]])],"derivedFrom":subQ3}),-1.0]])]});}
            var Q14;
            {var subQ5=sQuery(id+"F2.wireOp",EDGE,"E537");Q14=makeQuery(id+"F2.imprint","IMPRINT",FACE,{"disambiguationData":[TD([[makeQuery(id+"F2.imprint","IMPRINT",EDGE,{"derivedFrom":subQ5}),-1.0]])]});}
            var Q15;
            {var subQ3=sQuery(id+"F2.wireOp",EDGE,"E538");var subQ5=sQuery(id+"F2.wireOp",EDGE,"E539");var subQ7=makeQuery(id+"F2.imprint","INTERSECT",VERTEX,{"derivedFrom":[subQ3,subQ5]});Q15=makeQuery(id+"F2.imprint","IMPRINT",FACE,{"disambiguationData":[TD([[makeQuery(id+"F2.imprint","IMPRINT",EDGE,{"disambiguationData":[TD([[subQ7,1.0]])],"derivedFrom":subQ3}),-1.0]])]});}
            var Q16;
            {var subQ5=sQuery(id+"F2.wireOp",EDGE,"E540");Q16=makeQuery(id+"F2.imprint","IMPRINT",FACE,{"disambiguationData":[TD([[makeQuery(id+"F2.imprint","IMPRINT",EDGE,{"derivedFrom":subQ5}),-1.0]])]});}
            var Q17;
            {var subQ3=sQuery(id+"F2.wireOp",EDGE,"E541");var subQ5=sQuery(id+"F2.wireOp",EDGE,"E542");var subQ6=makeQuery(id+"F2.imprint","INTERSECT",VERTEX,{"derivedFrom":[subQ3,subQ5]});Q17=makeQuery(id+"F2.imprint","IMPRINT",FACE,{"disambiguationData":[TD([[makeQuery(id+"F2.imprint","IMPRINT",EDGE,{"disambiguationData":[TD([[subQ6,1.0]])],"derivedFrom":subQ3}),-1.0]])]});}
            var Q18;
            {var subQ5=sQuery(id+"F2.wireOp",EDGE,"E480");Q18=makeQuery(id+"F2.imprint","IMPRINT",FACE,{"disambiguationData":[TD([[makeQuery(id+"F2.imprint","IMPRINT",EDGE,{"derivedFrom":subQ5}),-1.0]])]});}
            var Q19;
            {var subQ5=sQuery(id+"F2.wireOp",EDGE,"E482");Q19=makeQuery(id+"F2.imprint","IMPRINT",FACE,{"disambiguationData":[TD([[makeQuery(id+"F2.imprint","IMPRINT",EDGE,{"derivedFrom":subQ5}),-1.0]])]});}
            var Q20;
            {var subQ5=sQuery(id+"F2.wireOp",EDGE,"E483");Q20=makeQuery(id+"F2.imprint","IMPRINT",FACE,{"disambiguationData":[TD([[makeQuery(id+"F2.imprint","IMPRINT",EDGE,{"derivedFrom":subQ5}),-1.0]])]});}
            var Q21;
            {var subQ5=sQuery(id+"F2.wireOp",EDGE,"E485");Q21=makeQuery(id+"F2.imprint","IMPRINT",FACE,{"disambiguationData":[TD([[makeQuery(id+"F2.imprint","IMPRINT",EDGE,{"derivedFrom":subQ5}),-1.0]])]});}
            var Q22;
            {var subQ0=sQuery(id+"F2.wireOp",EDGE,"E512");Q22=makeQuery(id+"F2.imprint","IMPRINT",FACE,{"disambiguationData":[TD([[makeQuery(id+"F2.imprint","IMPRINT",EDGE,{"derivedFrom":subQ0}),1.0]])]});}
            var Q23;
            {var subQ0=sQuery(id+"F2.wireOp",EDGE,"E512");Q23=makeQuery(id+"F2.imprint","IMPRINT",FACE,{"disambiguationData":[TD([[makeQuery(id+"F2.imprint","IMPRINT",EDGE,{"derivedFrom":subQ0}),-1.0]])]});}
            var Q24;
            {var subQ3=sQuery(id+"F2.wireOp",EDGE,"E502");Q24=makeQuery(id+"F2.imprint","IMPRINT",FACE,{"disambiguationData":[TD([[makeQuery(id+"F2.imprint","IMPRINT",EDGE,{"derivedFrom":subQ3}),1.0]])]});}
            var Q25;
            {var subQ0=sQuery(id+"F2.wireOp",EDGE,"E510");Q25=makeQuery(id+"F2.imprint","IMPRINT",FACE,{"disambiguationData":[TD([[makeQuery(id+"F2.imprint","IMPRINT",EDGE,{"derivedFrom":subQ0}),1.0]])]});}
            var Q26;
            {var subQ3=sQuery(id+"F2.wireOp",EDGE,"E508");var subQ5=sQuery(id+"F2.wireOp",EDGE,"E509");var subQ6=makeQuery(id+"F2.imprint","INTERSECT",VERTEX,{"derivedFrom":[subQ3,subQ5]});Q26=makeQuery(id+"F2.imprint","IMPRINT",FACE,{"disambiguationData":[TD([[makeQuery(id+"F2.imprint","IMPRINT",EDGE,{"disambiguationData":[TD([[subQ6,1.0]])],"derivedFrom":subQ3}),1.0]])]});}
            var Q27;
            {var subQ3=sQuery(id+"F2.wireOp",EDGE,"E470");Q27=makeQuery(id+"F2.imprint","IMPRINT",FACE,{"disambiguationData":[TD([[makeQuery(id+"F2.imprint","IMPRINT",EDGE,{"derivedFrom":subQ3}),1.0]])]});}
            var Q28;
            {var subQ1=sQuery(id+"F2.wireOp",EDGE,"E486");Q28=makeQuery(id+"F2.imprint","IMPRINT",FACE,{"disambiguationData":[TD([[makeQuery(id+"F2.imprint","IMPRINT",EDGE,{"derivedFrom":subQ1}),-1.0]])]});}
            var Q29;
            {var subQ0=sQuery(id+"F2.wireOp",EDGE,"E463");Q29=makeQuery(id+"F2.imprint","IMPRINT",FACE,{"disambiguationData":[TD([[makeQuery(id+"F2.imprint","IMPRINT",EDGE,{"derivedFrom":subQ0}),1.0]])]});}
            var Q30;
            {var subQ0=sQuery(id+"F2.wireOp",EDGE,"E464");Q30=makeQuery(id+"F2.imprint","IMPRINT",FACE,{"disambiguationData":[TD([[makeQuery(id+"F2.imprint","IMPRINT",EDGE,{"derivedFrom":subQ0}),1.0]])]});}
            var Q31;
            {var subQ4=sQuery(id+"F2.wireOp",EDGE,"E465");Q31=makeQuery(id+"F2.imprint","IMPRINT",FACE,{"disambiguationData":[TD([[makeQuery(id+"F2.imprint","IMPRINT",EDGE,{"derivedFrom":subQ4}),1.0]])]});}
            var Q32;
            {var subQ0=sQuery(id+"F2.wireOp",EDGE,"E466");Q32=makeQuery(id+"F2.imprint","IMPRINT",FACE,{"disambiguationData":[TD([[makeQuery(id+"F2.imprint","IMPRINT",EDGE,{"derivedFrom":subQ0}),1.0]])]});}
            var Q33;
            {var subQ3=sQuery(id+"F2.wireOp",EDGE,"E467");Q33=makeQuery(id+"F2.imprint","IMPRINT",FACE,{"disambiguationData":[TD([[makeQuery(id+"F2.imprint","IMPRINT",EDGE,{"derivedFrom":subQ3}),1.0]])]});}
            var Q34;
            {var subQ0=sQuery(id+"F2.wireOp",EDGE,"E468");Q34=makeQuery(id+"F2.imprint","IMPRINT",FACE,{"disambiguationData":[TD([[makeQuery(id+"F2.imprint","IMPRINT",EDGE,{"derivedFrom":subQ0}),1.0]])]});}
            var Q35;
            {var subQ0=sQuery(id+"F2.wireOp",EDGE,"E469");Q35=makeQuery(id+"F2.imprint","IMPRINT",FACE,{"disambiguationData":[TD([[makeQuery(id+"F2.imprint","IMPRINT",EDGE,{"derivedFrom":subQ0}),1.0]])]});}
            var Q36;
            {var subQ0=sQuery(id+"F2.wireOp",EDGE,"E471");Q36=makeQuery(id+"F2.imprint","IMPRINT",FACE,{"disambiguationData":[TD([[makeQuery(id+"F2.imprint","IMPRINT",EDGE,{"derivedFrom":subQ0}),1.0]])]});}
            var Q37;
            {var subQ0=sQuery(id+"F2.wireOp",EDGE,"E472");Q37=makeQuery(id+"F2.imprint","IMPRINT",FACE,{"disambiguationData":[TD([[makeQuery(id+"F2.imprint","IMPRINT",EDGE,{"derivedFrom":subQ0}),1.0]])]});}
            var Q38;
            {var subQ4=sQuery(id+"F2.wireOp",EDGE,"E473");Q38=makeQuery(id+"F2.imprint","IMPRINT",FACE,{"disambiguationData":[TD([[makeQuery(id+"F2.imprint","IMPRINT",EDGE,{"derivedFrom":subQ4}),1.0]])]});}
            var Q39;
            {var subQ0=sQuery(id+"F2.wireOp",EDGE,"E496");Q39=makeQuery(id+"F2.imprint","IMPRINT",FACE,{"disambiguationData":[TD([[makeQuery(id+"F2.imprint","IMPRINT",EDGE,{"derivedFrom":subQ0}),-1.0]])]});}
            var Q40;
            {var subQ0=sQuery(id+"F2.wireOp",EDGE,"E495");Q40=makeQuery(id+"F2.imprint","IMPRINT",FACE,{"disambiguationData":[TD([[makeQuery(id+"F2.imprint","IMPRINT",EDGE,{"derivedFrom":subQ0}),-1.0]])]});}
            var Q41;
            {var subQ2=sQuery(id+"F2.wireOp",EDGE,"E493");Q41=makeQuery(id+"F2.imprint","IMPRINT",FACE,{"disambiguationData":[TD([[makeQuery(id+"F2.imprint","IMPRINT",EDGE,{"derivedFrom":subQ2}),-1.0]])]});}
            var Q42;
            {var subQ0=sQuery(id+"F2.wireOp",EDGE,"E494");Q42=makeQuery(id+"F2.imprint","IMPRINT",FACE,{"disambiguationData":[TD([[makeQuery(id+"F2.imprint","IMPRINT",EDGE,{"derivedFrom":subQ0}),-1.0]])]});}
            var Q43;
            {var subQ0=sQuery(id+"F2.wireOp",EDGE,"E492");Q43=makeQuery(id+"F2.imprint","IMPRINT",FACE,{"disambiguationData":[TD([[makeQuery(id+"F2.imprint","IMPRINT",EDGE,{"derivedFrom":subQ0}),-1.0]])]});}
            var Q44;
            {var subQ0=sQuery(id+"F2.wireOp",EDGE,"E487");Q44=makeQuery(id+"F2.imprint","IMPRINT",FACE,{"disambiguationData":[TD([[makeQuery(id+"F2.imprint","IMPRINT",EDGE,{"derivedFrom":subQ0}),-1.0]])]});}
            var Q45;
            {var subQ0=sQuery(id+"F2.wireOp",EDGE,"E488");Q45=makeQuery(id+"F2.imprint","IMPRINT",FACE,{"disambiguationData":[TD([[makeQuery(id+"F2.imprint","IMPRINT",EDGE,{"derivedFrom":subQ0}),-1.0]])]});}
            var Q46;
            {var subQ0=sQuery(id+"F2.wireOp",EDGE,"E489");Q46=makeQuery(id+"F2.imprint","IMPRINT",FACE,{"disambiguationData":[TD([[makeQuery(id+"F2.imprint","IMPRINT",EDGE,{"derivedFrom":subQ0}),-1.0]])]});}
            var Q47;
            {var subQ2=sQuery(id+"F2.wireOp",EDGE,"E490");Q47=makeQuery(id+"F2.imprint","IMPRINT",FACE,{"disambiguationData":[TD([[makeQuery(id+"F2.imprint","IMPRINT",EDGE,{"derivedFrom":subQ2}),-1.0]])]});}
            var Q48;
            {var subQ0=sQuery(id+"F2.wireOp",EDGE,"E491");Q48=makeQuery(id+"F2.imprint","IMPRINT",FACE,{"disambiguationData":[TD([[makeQuery(id+"F2.imprint","IMPRINT",EDGE,{"derivedFrom":subQ0}),-1.0]])]});}
            var Q49;
            {var subQ0=sQuery(id+"F2.wireOp",EDGE,"E474");Q49=makeQuery(id+"F2.imprint","IMPRINT",FACE,{"disambiguationData":[TD([[makeQuery(id+"F2.imprint","IMPRINT",EDGE,{"derivedFrom":subQ0}),1.0]])]});}
            var Q50;
            {var subQ2=sQuery(id+"F2.wireOp",EDGE,"E497");Q50=makeQuery(id+"F2.imprint","IMPRINT",FACE,{"disambiguationData":[TD([[makeQuery(id+"F2.imprint","IMPRINT",EDGE,{"derivedFrom":subQ2}),-1.0]])]});}
            extrude(context, id + "F3", {"entities" : qUnion([Q0, Q1, Q2, Q3, Q4, Q5, Q6, Q7, Q8, Q9, Q10, Q11, Q12, Q13, Q14, Q15, Q16, Q17, Q18, Q19, Q20, Q21, Q22, Q23, Q24, Q25, Q26, Q27, Q28, Q29, Q30, Q31, Q32, Q33, Q34, Q35, Q36, Q37, Q38, Q39, Q40, Q41, Q42, Q43, Q44, Q45, Q46, Q47, Q48, Q49, Q50]), "depth" : 15 * mm});
        }
    });
